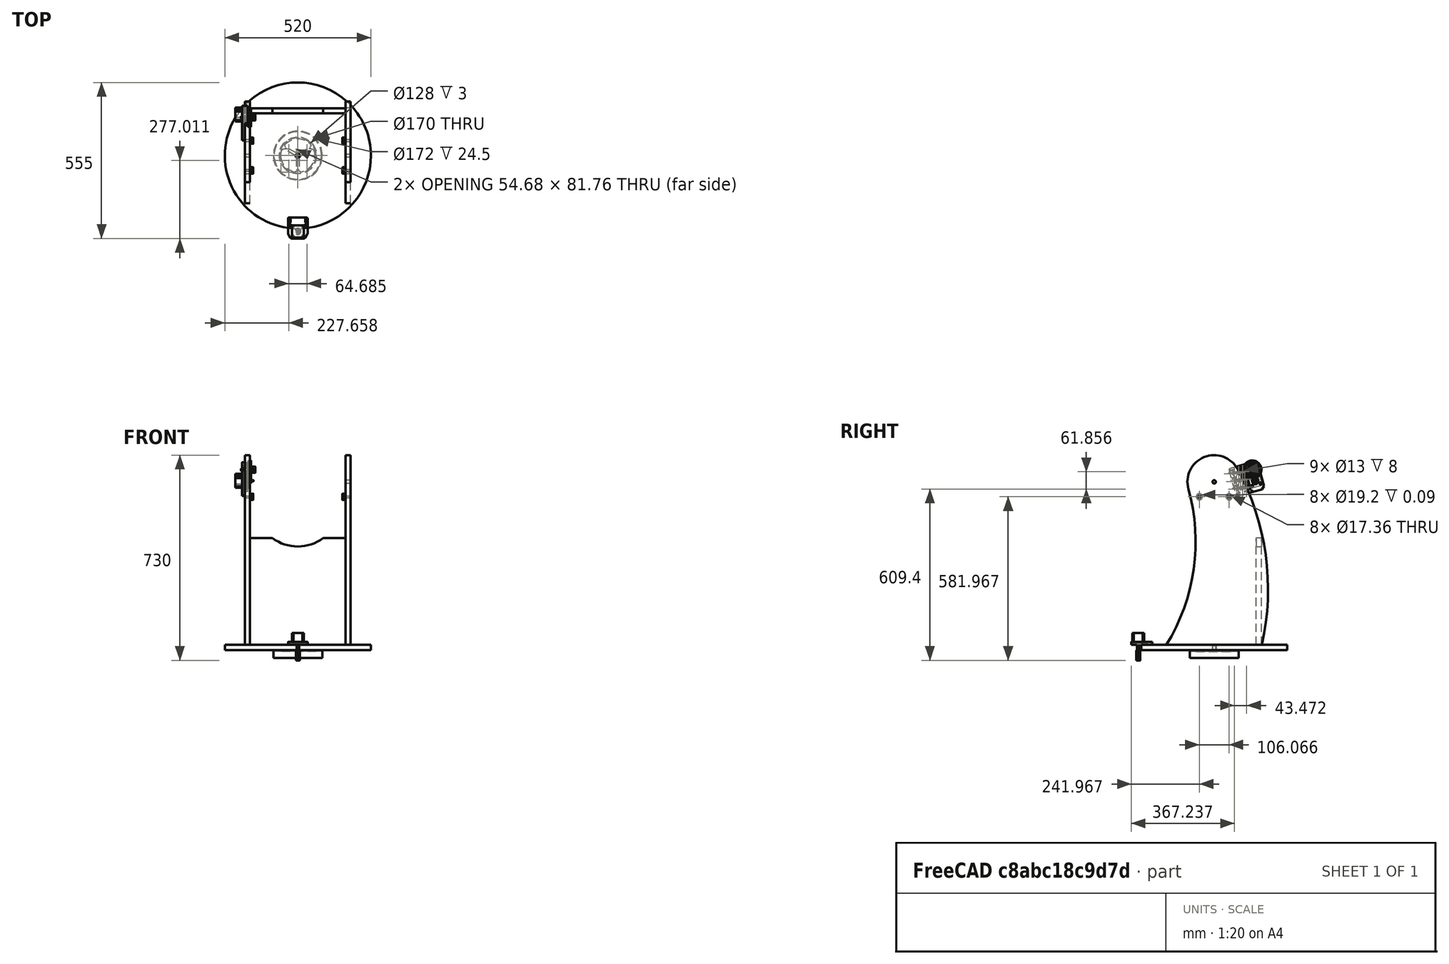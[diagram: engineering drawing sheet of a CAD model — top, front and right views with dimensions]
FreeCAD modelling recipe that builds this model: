
FCSTD DOCUMENT  (FreeCAD 2020.12.13R23076 +3015 (Git))
Label: zawieszenia-gora
License: All rights reserved
LicenseURL: http://en.wikipedia.org/wiki/All_rights_reserved
objects: App::FeaturePython×116, Part::FeaturePython×97, App::Link×24
note: 96 computed .brp shape members not serialized (recipe doc carries the construction recipe); baked Part::Feature solids carry a one-line shape summary decoded from their .brp
EXTERNAL_REF file=plyta-okr-gora.fcstd obj=Body
EXTERNAL_REF file=plyta-tylna.fcstd obj=Body
EXTERNAL_REF file=plyta-boczna.fcstd obj=Body
EXTERNAL_REF file=krokowiec-dol.FCStd obj=Body
EXTERNAL_REF file=krokowiec-nema17.FCStd obj=Body
EXTERNAL_REF file=kolkozebmodul1fi5sc.FCStd obj=Body
EXTERNAL_REF file=przekladnia.FCStd obj=Assembly
EXTERNAL_REF file=tulejka-sruby.FCStd obj=Body
EXTERNAL_REF file=piasta-lozyska2.FCStd obj=Body
EXTERNAL_REF file=oslona-lozyska.FCStd obj=Body
EXTERNAL_REF file=dystans-lozyska.FCStd obj=Body
EXTERNAL_REF file=lozysko 608.FCStd obj=Assembly

FEATURE [App::Link] Link  label="Link_plyta-okr-gora"
  LinkPlacement = pos=(-111,-1.99997,195) rot=(0,0,1;0rad)
  LinkedObject = -> <external plyta-okr-gora.fcstd>#Body
  Placement = pos=(-111,-1.99997,195) rot=(0,0,1;0rad)
  SyncGroupVisibility = false
  _LinkVersion = 1
FEATURE [App::Link] Link001  label="Link001_Assembly"
  LinkedObject = -> Assembly
  SyncGroupVisibility = false
  _LinkVersion = 1
FEATURE [App::Link] Link002  label="Link002_plyta-tylna"
  LinkPlacement = pos=(-111,166,213) rot=(0,0,1;0rad)
  LinkedObject = -> <external plyta-tylna.fcstd>#Body
  Placement = pos=(-111,166,213) rot=(0,0,1;0rad)
  SyncGroupVisibility = false
  _LinkVersion = 1
FEATURE [App::Link] Link003  label="Link003_Assembly"
  LinkedObject = -> Assembly
  SyncGroupVisibility = false
  _LinkVersion = 1
FEATURE [Part::FeaturePython] Element  # link proxy (typed FeaturePython)
  Detach = false
  LinkTransform = true
  LinkedObject = -> Link [Pad.Face2]
  _LinkVersion = 1
FEATURE [Part::FeaturePython] Element001  # link proxy (typed FeaturePython)
  Detach = false
  LinkTransform = true
  LinkedObject = -> Link002 [Pad.Face1]
  _LinkVersion = 1
FEATURE [Part::FeaturePython] Element002  # link proxy (typed FeaturePython)
  Detach = false
  LinkTransform = true
  LinkedObject = -> Link [Pad.Face3]
  _LinkVersion = 1
FEATURE [Part::FeaturePython] Element003  # link proxy (typed FeaturePython)
  Detach = false
  LinkTransform = true
  LinkedObject = -> Link [Origin.YZ_Plane.]
  _LinkVersion = 1
FEATURE [Part::FeaturePython] Element004  # link proxy (typed FeaturePython)
  Detach = false
  LinkTransform = true
  LinkedObject = -> Link002 [Origin.YZ_Plane.]
  _LinkVersion = 1
FEATURE [Part::FeaturePython] Element005  # link proxy (typed FeaturePython)
  Detach = false
  LinkTransform = true
  LinkedObject = -> Link002 [Origin.XY_Plane.]
  _LinkVersion = 1
FEATURE [Part::FeaturePython] Element006  # link proxy (typed FeaturePython)
  Detach = false
  LinkTransform = true
  LinkedObject = -> Link002 [Pad.Face8]
  _LinkVersion = 1
FEATURE [Part::FeaturePython] Element007  # link proxy (typed FeaturePython)
  Detach = false
  LinkTransform = true
  LinkedObject = -> Link [Origin.XZ_Plane.]
  _LinkVersion = 1
FEATURE [App::Link] Link004  label="Link004_Assembly"
  LinkedObject = -> Assembly
  SyncGroupVisibility = false
  _LinkVersion = 1
FEATURE [App::Link] Link005  label="Link005_plyta-boczna"
  LinkPlacement = pos=(68.0001,-1.99997,213) rot=(0,0,1;0rad)
  LinkedObject = -> <external plyta-boczna.fcstd>#Body
  Placement = pos=(68.0001,-1.99997,213) rot=(0,0,1;0rad)
  SyncGroupVisibility = false
  _LinkVersion = 1
FEATURE [Part::FeaturePython] Element008  # link proxy (typed FeaturePython)
  Detach = false
  LinkTransform = true
  LinkedObject = -> Link005 [Pad.Face6]
  _LinkVersion = 1
FEATURE [Part::FeaturePython] Element009  # link proxy (typed FeaturePython)
  Detach = false
  LinkTransform = true
  LinkedObject = -> Link002 [Pad.Face2]
  _LinkVersion = 1
FEATURE [Part::FeaturePython] Element010  # link proxy (typed FeaturePython)
  Detach = false
  LinkTransform = true
  LinkedObject = -> Link005 [Origin.XY_Plane.]
  _LinkVersion = 1
FEATURE [Part::FeaturePython] Element011  # link proxy (typed FeaturePython)
  Detach = false
  LinkTransform = true
  LinkedObject = -> Link005 [Origin.XZ_Plane.]
  _LinkVersion = 1
FEATURE [App::Link] Link006  label="Link006_Assembly"
  LinkedObject = -> Assembly
  SyncGroupVisibility = false
  _LinkVersion = 1
FEATURE [App::Link] Link007  label="Link007_plyta-boczna"
  LinkPlacement = pos=(-290,-1.99997,213) rot=(0,0,1;0rad)
  LinkedObject = -> <external plyta-boczna.fcstd>#Body
  Placement = pos=(-290,-1.99997,213) rot=(0,0,1;0rad)
  SyncGroupVisibility = false
  _LinkVersion = 1
FEATURE [Part::FeaturePython] Element012  # link proxy (typed FeaturePython)
  Detach = false
  LinkTransform = true
  LinkedObject = -> Link007 [Pad.Face7]
  _LinkVersion = 1
FEATURE [Part::FeaturePython] Element013  # link proxy (typed FeaturePython)
  Detach = false
  LinkTransform = true
  LinkedObject = -> Link002 [Pad.Face6]
  _LinkVersion = 1
FEATURE [Part::FeaturePython] Element014  # link proxy (typed FeaturePython)
  Detach = false
  LinkTransform = true
  LinkedObject = -> Link007 [Origin.XY_Plane.]
  _LinkVersion = 1
FEATURE [Part::FeaturePython] Element015  # link proxy (typed FeaturePython)
  Detach = false
  LinkTransform = true
  LinkedObject = -> Link007 [Origin.XZ_Plane.]
  _LinkVersion = 1
FEATURE [App::Link] Link009  label="Link009_zawieszenie-gora"
  LinkedObject = -> Assembly
  SyncGroupVisibility = false
  _LinkVersion = 1
FEATURE [Part::FeaturePython] Element017  # link proxy (typed FeaturePython)
  Detach = false
  LinkTransform = true
  LinkedObject = -> Link005 [Pocket.Face9]
  _LinkVersion = 1
FEATURE [Part::FeaturePython] Element019  # link proxy (typed FeaturePython)
  Detach = false
  LinkTransform = true
  LinkedObject = -> Link005 [Pocket.Face4]
  _LinkVersion = 1
FEATURE [Part::FeaturePython] Element020  # link proxy (typed FeaturePython)
  Detach = false
  LinkTransform = true
  LinkedObject = -> Link005 [Pocket.Face8]
  _LinkVersion = 1
FEATURE [Part::FeaturePython] Element024  # link proxy (typed FeaturePython)
  Detach = false
  LinkTransform = true
  LinkedObject = -> Link005 [Pocket.Face1]
  _LinkVersion = 1
FEATURE [App::Link] Link010  label="krokowiec-dol"
  LinkPlacement = pos=(-111,-272,213) rot=(0,0,1;0rad)
  LinkedObject = -> <external krokowiec-dol.FCStd>#Body
  Placement = pos=(-111,-272,213) rot=(0,0,1;0rad)
  SyncGroupVisibility = false
  _LinkVersion = 1
FEATURE [App::Link] Link011  label="nema17"
  LinkPlacement = pos=(-111,-272,256) rot=(1,0,0;3.14159rad)
  LinkedObject = -> <external krokowiec-nema17.FCStd>#Body
  Placement = pos=(-111,-272,256) rot=(1,0,0;3.14159rad)
  SyncGroupVisibility = false
  _LinkVersion = 1
FEATURE [App::Link] Link012  label="kolkozebstoz"
  LinkPlacement = pos=(-111,-272,158) rot=(0,0,1;0rad)
  LinkedObject = -> <external kolkozebmodul1fi5sc.FCStd>#Body
  Placement = pos=(-111,-272,158) rot=(0,0,1;0rad)
  SyncGroupVisibility = false
  _LinkVersion = 1
FEATURE [App::Link] Link016  label="przekladnia"
  LinkPlacement = pos=(-309,143.893,797.746) rot=(-0.704063,-0.092692,0.704063;2.95674rad)
  LinkedObject = -> <external przekladnia.FCStd>#Assembly
  Placement = pos=(-309,143.893,797.746) rot=(-0.704063,-0.092692,0.704063;2.95674rad)
  SyncGroupVisibility = false
  _LinkVersion = 1
FEATURE [App::Link] Link017  label="tulejka-sruby"
  LinkPlacement = pos=(-111,-1.99997,195) rot=(0,0,1;0rad)
  LinkedObject = -> <external tulejka-sruby.FCStd>#Body
  Placement = pos=(-111,-1.99997,195) rot=(0,0,1;0rad)
  SyncGroupVisibility = false
  _LinkVersion = 1
FEATURE [App::Link] Link018  label="piasta-lozyska2"
  LinkPlacement = pos=(-111,-1.99997,195) rot=(1,0,0;3.14159rad)
  LinkedObject = -> <external piasta-lozyska2.FCStd>#Body
  Placement = pos=(-111,-1.99997,195) rot=(1,0,0;3.14159rad)
  SyncGroupVisibility = false
  _LinkVersion = 1
FEATURE [App::Link] Link019  label="oslona-lozyska"
  LinkPlacement = pos=(-111,-1.99997,166) rot=(0,0,1;0rad)
  LinkedObject = -> <external oslona-lozyska.FCStd>#Body
  Placement = pos=(-111,-1.99997,166) rot=(0,0,1;0rad)
  SyncGroupVisibility = false
  _LinkVersion = 1
FEATURE [App::Link] Link020  label="dystans-lozyska"
  LinkPlacement = pos=(-281,-55.033,739.967) rot=(0.678598,0.281085,0.678598;2.59356rad)
  LinkedObject = -> <external dystans-lozyska.FCStd>#Body
  Placement = pos=(-281,-55.033,739.967) rot=(0.678598,0.281085,0.678598;2.59356rad)
  SyncGroupVisibility = false
  _LinkVersion = 1
FEATURE [App::Link] Link021  label="dystans-lozyska001"
  LinkPlacement = pos=(-281,51.033,739.967) rot=(0.678598,-0.281085,0.678598;3.68962rad)
  LinkedObject = -> Link020
  Placement = pos=(-281,51.033,739.967) rot=(0.678598,-0.281085,0.678598;3.68962rad)
  SyncGroupVisibility = false
  _LinkVersion = 1
FEATURE [App::Link] Link022  label="dystans-lozyska002"
  LinkPlacement = pos=(59.0001,-55.033,739.967) rot=(-0.357407,-0.862856,0.357407;1.71777rad)
  LinkedObject = -> Link020
  Placement = pos=(59.0001,-55.033,739.967) rot=(-0.357407,-0.862856,0.357407;1.71777rad)
  SyncGroupVisibility = false
  _LinkVersion = 1
FEATURE [App::Link] Link023  label="dystans-lozyska003"
  LinkPlacement = pos=(59.0001,51.033,739.967) rot=(-0.357407,0.862856,0.357407;4.56541rad)
  LinkedObject = -> Link020
  Placement = pos=(59.0001,51.033,739.967) rot=(-0.357407,0.862856,0.357407;4.56541rad)
  SyncGroupVisibility = false
  _LinkVersion = 1
FEATURE [App::Link] Link024  label="608-2RS"
  LinkPlacement = pos=(-277,-55.033,739.967) rot=(0,0,1;0rad)
  LinkedObject = -> <external lozysko 608.FCStd>#Assembly
  Placement = pos=(-277,-55.033,739.967) rot=(0,0,1;0rad)
  SyncGroupVisibility = false
  _LinkVersion = 1
FEATURE [App::Link] Link026  label="608-2RS002"
  LinkPlacement = pos=(-277,51.033,739.967) rot=(0,0,1;0rad)
  LinkedObject = -> Link024
  Placement = pos=(-277,51.033,739.967) rot=(0,0,1;0rad)
  SyncGroupVisibility = false
  _LinkVersion = 1
FEATURE [App::Link] Link027  label="608-2RS003"
  LinkPlacement = pos=(55.0001,-55.033,739.967) rot=(0,1,0;3.14159rad)
  LinkedObject = -> Link024
  Placement = pos=(55.0001,-55.033,739.967) rot=(0,1,0;3.14159rad)
  SyncGroupVisibility = false
  _LinkVersion = 1
FEATURE [App::Link] Link028  label="608-2RS004"
  LinkPlacement = pos=(55.0001,51.033,739.967) rot=(0,1,0;3.14159rad)
  LinkedObject = -> Link024
  Placement = pos=(55.0001,51.033,739.967) rot=(0,1,0;3.14159rad)
  SyncGroupVisibility = false
  _LinkVersion = 1
FEATURE [Part::FeaturePython] Parts  # WARN: FeaturePython — macro-defined, semantics opaque (R4)
  Group = -> [Link,Link002,Link005,Link007,Link010,Link011,Link012,Link016,Link017,Link018,Link019,Link020,Link021,Link022,Link023,Link024,Link026,Link027,Link028]
  GroupMode = 0
  _LinkVersion = 1
FEATURE [Part::FeaturePython] Assembly  label="zawieszenie-gora"  # WARN: FeaturePython — macro-defined, semantics opaque (R4)
  AutoRelax = true
  BuildShape = 0
  Freeze = true
  Group = -> [Constraints,Elements,Parts]
  Verbose = false
  _LinkVersion = 1
  _SolverType = 1
FEATURE [App::FeaturePython] Constraints  # WARN: FeaturePython — macro-defined, semantics opaque (R4)
  Group = -> [Constraint,Constraint001,Constraint002,Constraint003,Constraint004,Constraint005,Constraint006,Constraint007,Constraint008,Constraint013,Constraint014,Constraint015,Constraint022,Constraint023,Constraint024,Constraint025,Constraint026,Constraint027,Constraint028,Constraint029,Constraint030,Constraint031,Constraint032,Constraint033,Constraint034,Constraint035,Constraint036,Constraint037,+10 more]
  _LinkVersion = 1
  _Version = 1
FEATURE [App::FeaturePython] Elements  # WARN: FeaturePython — macro-defined, semantics opaque (R4)
  Group = -> [Element,Element001,Element002,Element003,Element004,Element005,Element006,Element007,Element008,Element009,Element010,Element011,Element012,Element013,Element014,Element015,Element017,Element019,Element020,Element024,Element025,Element026,Element027,Element028,_Element,_Element001,_Element002,_Element003,_Element004,_Element005,_Element006,_Element007,_Element008,Element029,Element030,Element031,+59 more]
  _LinkVersion = 1
FEATURE [Part::FeaturePython] Element025  # link proxy (typed FeaturePython)
  Detach = false
  LinkTransform = true
  LinkedObject = -> Link [Pocket.Face4]
  _LinkVersion = 1
  _Parent = -> Elements
FEATURE [Part::FeaturePython] Element026  # link proxy (typed FeaturePython)
  Detach = false
  LinkTransform = true
  LinkedObject = -> Link [Pocket.Edge4]
  _LinkVersion = 1
  _Parent = -> Elements
FEATURE [Part::FeaturePython] Element027  # link proxy (typed FeaturePython)
  Detach = false
  LinkTransform = true
  LinkedObject = -> Link [Pocket.Face2]
  _LinkVersion = 1
  _Parent = -> Elements
FEATURE [Part::FeaturePython] Element028  # link proxy (typed FeaturePython)
  Detach = false
  LinkTransform = true
  LinkedObject = -> Link007 [Pocket.Edge17]
  _LinkVersion = 1
  _Parent = -> Elements
FEATURE [App::FeaturePython] Constraint  label="PlaneAlignment"  # WARN: FeaturePython — macro-defined, semantics opaque (R4)
  Angle = 0
  AnglePitch = 0
  AngleRoll = 0
  Cascade = false
  Disabled = false
  Group = -> [ElementLink,ElementLink001]
  LockAngle = false
  _ConstraintType = 37
  _LinkVersion = 1
  _Parent = -> Constraints
FEATURE [App::FeaturePython] ElementLink  label="Element001"  # link proxy (typed FeaturePython)
  LinkTransform = true
  LinkedObject = -> Element001
  _LinkVersion = 1
  _Parent = -> Constraint
FEATURE [App::FeaturePython] ElementLink001  label="_Element"  # link proxy (typed FeaturePython)
  LinkTransform = true
  LinkedObject = -> _Element
  _LinkVersion = 1
  _Parent = -> Constraint
FEATURE [Part::FeaturePython] _Element  # link proxy (typed FeaturePython)
  Detach = false
  LinkTransform = true
  LinkedObject = -> Link [Pocket.Face3]
  _LinkVersion = 1
  _Parent = -> Elements
FEATURE [Part::FeaturePython] _Element001  # link proxy (typed FeaturePython)
  Detach = false
  LinkTransform = true
  LinkedObject = -> Link [Sketch002.Edge2]
  _LinkVersion = 1
  _Parent = -> Elements
FEATURE [Part::FeaturePython] _Element002  # link proxy (typed FeaturePython)
  Detach = false
  LinkTransform = true
  LinkedObject = -> Link [Sketch002.Vertex1]
  _LinkVersion = 1
  _Parent = -> Elements
FEATURE [App::FeaturePython] Constraint001  label="PointInPlane"  # WARN: FeaturePython — macro-defined, semantics opaque (R4)
  Disabled = false
  Group = -> [ElementLink002,ElementLink003]
  _ConstraintType = 3
  _LinkVersion = 1
  _Parent = -> Constraints
FEATURE [App::FeaturePython] ElementLink002  label="_Element002"  # link proxy (typed FeaturePython)
  LinkTransform = true
  LinkedObject = -> _Element002
  _LinkVersion = 1
  _Parent = -> Constraint001
FEATURE [App::FeaturePython] ElementLink003  label="Element006"  # link proxy (typed FeaturePython)
  LinkTransform = true
  LinkedObject = -> Element006
  _LinkVersion = 1
  _Parent = -> Constraint001
FEATURE [App::FeaturePython] Constraint002  label="PointInPlane001"  # WARN: FeaturePython — macro-defined, semantics opaque (R4)
  Disabled = false
  Group = -> [ElementLink004,ElementLink005]
  _ConstraintType = 3
  _LinkVersion = 1
  _Parent = -> Constraints
FEATURE [App::FeaturePython] ElementLink004  label="_Element003"  # link proxy (typed FeaturePython)
  LinkTransform = true
  LinkedObject = -> _Element003
  _LinkVersion = 1
  _Parent = -> Constraint002
FEATURE [Part::FeaturePython] _Element003  # link proxy (typed FeaturePython)
  Detach = false
  LinkTransform = true
  LinkedObject = -> Link [Sketch002.Vertex3]
  _LinkVersion = 1
  _Parent = -> Elements
FEATURE [App::FeaturePython] ElementLink005  label="Element006"  # link proxy (typed FeaturePython)
  LinkTransform = true
  LinkedObject = -> Element006
  _LinkVersion = 1
  _Parent = -> Constraint002
FEATURE [App::FeaturePython] Constraint003  label="PlaneAlignment001"  # WARN: FeaturePython — macro-defined, semantics opaque (R4)
  Angle = 0
  AnglePitch = 0
  AngleRoll = 0
  Cascade = false
  Disabled = false
  Group = -> [ElementLink006,ElementLink007]
  LockAngle = false
  _ConstraintType = 37
  _LinkVersion = 1
  _Parent = -> Constraints
FEATURE [App::FeaturePython] ElementLink006  label="_Element004"  # link proxy (typed FeaturePython)
  LinkTransform = true
  LinkedObject = -> _Element004
  _LinkVersion = 1
  _Parent = -> Constraint003
FEATURE [Part::FeaturePython] _Element004  # link proxy (typed FeaturePython)
  Detach = false
  LinkTransform = true
  LinkedObject = -> Link005 [Pocket.Face6]
  _LinkVersion = 1
  _Parent = -> Elements
FEATURE [App::FeaturePython] ElementLink007  label="_Element"  # link proxy (typed FeaturePython)
  LinkTransform = true
  LinkedObject = -> _Element
  _LinkVersion = 1
  _Parent = -> Constraint003
FEATURE [App::FeaturePython] Constraint004  label="PointOnLine"  # WARN: FeaturePython — macro-defined, semantics opaque (R4)
  Disabled = false
  Group = -> [ElementLink008,ElementLink009]
  _ConstraintType = 4
  _LinkVersion = 1
  _Parent = -> Constraints
FEATURE [App::FeaturePython] ElementLink008  label="_Element005"  # link proxy (typed FeaturePython)
  LinkTransform = true
  LinkedObject = -> _Element005
  _LinkVersion = 1
  _Parent = -> Constraint004
FEATURE [Part::FeaturePython] _Element005  # link proxy (typed FeaturePython)
  Detach = false
  LinkTransform = true
  LinkedObject = -> Link [Sketch002.Vertex2]
  _LinkVersion = 1
  _Parent = -> Elements
FEATURE [App::FeaturePython] ElementLink009  label="_Element006"  # link proxy (typed FeaturePython)
  LinkTransform = true
  LinkedObject = -> _Element006
  _LinkVersion = 1
  _Parent = -> Constraint004
FEATURE [Part::FeaturePython] _Element006  # link proxy (typed FeaturePython)
  Detach = false
  LinkTransform = true
  LinkedObject = -> Link007 [Sketch002.Edge1]
  _LinkVersion = 1
  _Parent = -> Elements
FEATURE [App::FeaturePython] Constraint005  label="PlaneAlignment002"  # WARN: FeaturePython — macro-defined, semantics opaque (R4)
  Angle = 0
  AnglePitch = 0
  AngleRoll = 0
  Cascade = false
  Disabled = false
  Group = -> [ElementLink010,ElementLink011]
  LockAngle = false
  _ConstraintType = 37
  _LinkVersion = 1
  _Parent = -> Constraints
FEATURE [App::FeaturePython] ElementLink010  label="_Element007"  # link proxy (typed FeaturePython)
  LinkTransform = true
  LinkedObject = -> _Element007
  _LinkVersion = 1
  _Parent = -> Constraint005
FEATURE [Part::FeaturePython] _Element007  # link proxy (typed FeaturePython)
  Detach = false
  LinkTransform = true
  LinkedObject = -> Link007 [Pocket.Face6]
  _LinkVersion = 1
  _Parent = -> Elements
FEATURE [App::FeaturePython] ElementLink011  label="_Element"  # link proxy (typed FeaturePython)
  LinkTransform = true
  LinkedObject = -> _Element
  _LinkVersion = 1
  _Parent = -> Constraint005
FEATURE [App::FeaturePython] Constraint006  label="AxialAlignment"  # WARN: FeaturePython — macro-defined, semantics opaque (R4)
  Angle = 0
  AnglePitch = 0
  AngleRoll = 0
  Disabled = false
  Group = -> [ElementLink012,ElementLink013]
  LockAngle = false
  Multiply = false
  _ConstraintType = 36
  _LinkVersion = 1
  _Parent = -> Constraints
FEATURE [App::FeaturePython] ElementLink012  label="_Element008"  # link proxy (typed FeaturePython)
  LinkTransform = true
  LinkedObject = -> _Element008
  _LinkVersion = 1
  _Parent = -> Constraint006
FEATURE [Part::FeaturePython] _Element008  # link proxy (typed FeaturePython)
  Detach = false
  LinkTransform = true
  LinkedObject = -> Link007 [Pocket.Face1]
  _LinkVersion = 1
  _Parent = -> Elements
FEATURE [App::FeaturePython] ElementLink013  label="Element024"  # link proxy (typed FeaturePython)
  LinkTransform = true
  LinkedObject = -> Element024
  _LinkVersion = 1
  _Parent = -> Constraint006
FEATURE [Part::FeaturePython] Element029  # link proxy (typed FeaturePython)
  Detach = false
  LinkTransform = true
  LinkedObject = -> Link007 [Pocket.Face8]
  _LinkVersion = 1
  _Parent = -> Elements
FEATURE [Part::FeaturePython] Element030  # link proxy (typed FeaturePython)
  Detach = false
  LinkTransform = true
  LinkedObject = -> Link007 [Pocket.Face5]
  _LinkVersion = 1
  _Parent = -> Elements
FEATURE [Part::FeaturePython] Element031  # link proxy (typed FeaturePython)
  Detach = false
  LinkTransform = true
  LinkedObject = -> Link007 [Sketch002.Vertex1]
  _LinkVersion = 1
  _Parent = -> Elements
FEATURE [App::FeaturePython] Constraint007  label="PointsCoincident"  # WARN: FeaturePython — macro-defined, semantics opaque (R4)
  Disabled = false
  Group = -> [ElementLink014,ElementLink015]
  _ConstraintType = 1
  _LinkVersion = 1
  _Parent = -> Constraints
FEATURE [App::FeaturePython] ElementLink014  label="_Element009"  # link proxy (typed FeaturePython)
  LinkTransform = true
  LinkedObject = -> _Element009
  _LinkVersion = 1
  _Parent = -> Constraint007
FEATURE [Part::FeaturePython] _Element009  # link proxy (typed FeaturePython)
  Detach = false
  LinkTransform = true
  LinkedObject = -> Link [Sketch002.Vertex6]
  _LinkVersion = 1
  _Parent = -> Elements
FEATURE [App::FeaturePython] ElementLink015  label="_Element010"  # link proxy (typed FeaturePython)
  LinkTransform = true
  LinkedObject = -> _Element010
  _LinkVersion = 1
  _Parent = -> Constraint007
FEATURE [Part::FeaturePython] _Element010  # link proxy (typed FeaturePython)
  Detach = false
  LinkTransform = true
  LinkedObject = -> Link010 [Sketch008.Vertex2]
  _LinkVersion = 1
  _Parent = -> Elements
FEATURE [App::FeaturePython] Constraint008  label="PointOnLine001"  # WARN: FeaturePython — macro-defined, semantics opaque (R4)
  Disabled = false
  Group = -> [ElementLink016,ElementLink017]
  _ConstraintType = 4
  _LinkVersion = 1
  _Parent = -> Constraints
FEATURE [App::FeaturePython] ElementLink016  label="_Element011"  # link proxy (typed FeaturePython)
  LinkTransform = true
  LinkedObject = -> _Element011
  _LinkVersion = 1
  _Parent = -> Constraint008
FEATURE [Part::FeaturePython] _Element011  # link proxy (typed FeaturePython)
  Detach = false
  LinkTransform = true
  LinkedObject = -> Link010 [Sketch008.Vertex1]
  _LinkVersion = 1
  _Parent = -> Elements
FEATURE [App::FeaturePython] ElementLink017  label="_Element012"  # link proxy (typed FeaturePython)
  LinkTransform = true
  LinkedObject = -> _Element012
  _LinkVersion = 1
  _Parent = -> Constraint008
FEATURE [Part::FeaturePython] _Element012  # link proxy (typed FeaturePython)
  Detach = false
  LinkTransform = true
  LinkedObject = -> Link [Sketch002.Edge4]
  _LinkVersion = 1
  _Parent = -> Elements
FEATURE [Part::FeaturePython] _Element013  # link proxy (typed FeaturePython)
  Detach = false
  LinkTransform = true
  LinkedObject = -> Link011 [Chamfer001.Face9]
  _LinkVersion = 1
  _Parent = -> Elements
FEATURE [Part::FeaturePython] _Element015  # link proxy (typed FeaturePython)
  Detach = false
  LinkTransform = true
  LinkedObject = -> Link011 [Chamfer001.Face13]
  _LinkVersion = 1
  _Parent = -> Elements
FEATURE [Part::FeaturePython] _Element018  # link proxy (typed FeaturePython)
  Detach = false
  LinkTransform = true
  LinkedObject = -> Link011 [Chamfer001.Face1]
  _LinkVersion = 1
  _Parent = -> Elements
FEATURE [Part::FeaturePython] _Element020  # link proxy (typed FeaturePython)
  Detach = false
  LinkTransform = true
  LinkedObject = -> Link012 [Groove.Face75]
  _LinkVersion = 1
  _Parent = -> Elements
FEATURE [Part::FeaturePython] _Element021  # link proxy (typed FeaturePython)
  Detach = false
  LinkTransform = true
  LinkedObject = -> Link011 [Chamfer001.Face21]
  _LinkVersion = 1
  _Parent = -> Elements
FEATURE [Part::FeaturePython] _Element022  # link proxy (typed FeaturePython)
  Detach = false
  LinkTransform = true
  LinkedObject = -> Link012 [Groove.Face78]
  _LinkVersion = 1
  _Parent = -> Elements
FEATURE [Part::FeaturePython] _Element023  # link proxy (typed FeaturePython)
  Detach = false
  LinkTransform = true
  LinkedObject = -> Link011 [Chamfer001.Face23]
  _LinkVersion = 1
  _Parent = -> Elements
FEATURE [Part::FeaturePython] _Element024  # link proxy (typed FeaturePython)
  Detach = false
  LinkTransform = true
  LinkedObject = -> Link012 [Groove.Face76]
  _LinkVersion = 1
  _Parent = -> Elements
FEATURE [Part::FeaturePython] _Element025  # link proxy (typed FeaturePython)
  Detach = false
  LinkTransform = true
  LinkedObject = -> Link011 [Chamfer001.Face22]
  _LinkVersion = 1
  _Parent = -> Elements
FEATURE [Part::FeaturePython] _Element026  # link proxy (typed FeaturePython)
  Detach = false
  LinkTransform = true
  LinkedObject = -> Link011 [Chamfer001.Vertex1]
  _LinkVersion = 1
  _Parent = -> Elements
FEATURE [App::FeaturePython] Constraint013  label="AxialAlignment002"  # WARN: FeaturePython — macro-defined, semantics opaque (R4)
  Angle = 0
  AnglePitch = 0
  AngleRoll = 0
  Disabled = false
  Group = -> [ElementLink026,ElementLink027]
  LockAngle = false
  Multiply = false
  _ConstraintType = 36
  _LinkVersion = 1
  _Parent = -> Constraints
FEATURE [App::FeaturePython] ElementLink026  label="_Element020"  # link proxy (typed FeaturePython)
  LinkTransform = true
  LinkedObject = -> _Element020
  _LinkVersion = 1
  _Parent = -> Constraint013
FEATURE [App::FeaturePython] ElementLink027  label="_Element021"  # link proxy (typed FeaturePython)
  LinkTransform = true
  LinkedObject = -> _Element021
  _LinkVersion = 1
  _Parent = -> Constraint013
FEATURE [App::FeaturePython] Constraint014  label="SameOrientation002"  # WARN: FeaturePython — macro-defined, semantics opaque (R4)
  Disabled = false
  Group = -> [ElementLink028,ElementLink029]
  _ConstraintType = 2
  _LinkVersion = 1
  _Parent = -> Constraints
FEATURE [App::FeaturePython] ElementLink028  label="_Element022"  # link proxy (typed FeaturePython)
  LinkTransform = true
  LinkedObject = -> _Element022
  _LinkVersion = 1
  _Parent = -> Constraint014
FEATURE [App::FeaturePython] ElementLink029  label="_Element023"  # link proxy (typed FeaturePython)
  LinkTransform = true
  LinkedObject = -> _Element023
  _LinkVersion = 1
  _Parent = -> Constraint014
FEATURE [App::FeaturePython] Constraint015  label="PointInPlane003"  # WARN: FeaturePython — macro-defined, semantics opaque (R4)
  Disabled = false
  Group = -> [ElementLink030,ElementLink031]
  _ConstraintType = 3
  _LinkVersion = 1
  _Parent = -> Constraints
FEATURE [App::FeaturePython] ElementLink030  label="_Element027"  # link proxy (typed FeaturePython)
  LinkTransform = true
  LinkedObject = -> _Element027
  _LinkVersion = 1
  _Parent = -> Constraint015
FEATURE [Part::FeaturePython] _Element027  # link proxy (typed FeaturePython)
  Detach = false
  LinkTransform = true
  LinkedObject = -> Link011 [Chamfer001.Vertex33]
  _LinkVersion = 1
  _Parent = -> Elements
FEATURE [App::FeaturePython] ElementLink031  label="_Element024"  # link proxy (typed FeaturePython)
  LinkTransform = true
  LinkedObject = -> _Element024
  _LinkVersion = 1
  _Parent = -> Constraint015
FEATURE [Part::FeaturePython] _Element033  # link proxy (typed FeaturePython)
  Detach = false
  LinkTransform = true
  LinkedObject = -> Link007 [Pocket.Face4]
  _LinkVersion = 1
  _Parent = -> Elements
FEATURE [App::FeaturePython] Constraint022  label="PointInPlane006"  # WARN: FeaturePython — macro-defined, semantics opaque (R4)
  Disabled = false
  Group = -> [ElementLink044,ElementLink045]
  _ConstraintType = 3
  _LinkVersion = 1
  _Parent = -> Constraints
FEATURE [App::FeaturePython] ElementLink044  label="_Element002"  # link proxy (typed FeaturePython)
  LinkTransform = true
  LinkedObject = -> _Element002
  _LinkVersion = 1
  _Parent = -> Constraint022
FEATURE [App::FeaturePython] ElementLink045  label="Element030"  # link proxy (typed FeaturePython)
  LinkTransform = true
  LinkedObject = -> Element030
  _LinkVersion = 1
  _Parent = -> Constraint022
FEATURE [App::FeaturePython] Constraint023  label="PlaneAlignment003"  # WARN: FeaturePython — macro-defined, semantics opaque (R4)
  Angle = 0
  AnglePitch = 0
  AngleRoll = 0
  Cascade = false
  Disabled = false
  Group = -> [ElementLink046,ElementLink047]
  LockAngle = false
  _ConstraintType = 37
  _LinkVersion = 1
  _Parent = -> Constraints
FEATURE [App::FeaturePython] ElementLink046  label="Element013"  # link proxy (typed FeaturePython)
  LinkTransform = true
  LinkedObject = -> Element013
  _LinkVersion = 1
  _Parent = -> Constraint023
FEATURE [App::FeaturePython] ElementLink047  label="Element030"  # link proxy (typed FeaturePython)
  LinkTransform = true
  LinkedObject = -> Element030
  _LinkVersion = 1
  _Parent = -> Constraint023
FEATURE [App::FeaturePython] Constraint024  label="PlaneAlignment004"  # WARN: FeaturePython — macro-defined, semantics opaque (R4)
  Angle = 0
  AnglePitch = 0
  AngleRoll = 0
  Cascade = false
  Disabled = false
  Group = -> [ElementLink048,ElementLink049]
  LockAngle = false
  _ConstraintType = 37
  _LinkVersion = 1
  _Parent = -> Constraints
FEATURE [App::FeaturePython] ElementLink048  label="Element019"  # link proxy (typed FeaturePython)
  LinkTransform = true
  LinkedObject = -> Element019
  _LinkVersion = 1
  _Parent = -> Constraint024
FEATURE [App::FeaturePython] ElementLink049  label="Element009"  # link proxy (typed FeaturePython)
  LinkTransform = true
  LinkedObject = -> Element009
  _LinkVersion = 1
  _Parent = -> Constraint024
FEATURE [Part::FeaturePython] _Element053  # link proxy (typed FeaturePython)
  Detach = false
  LinkTransform = true
  LinkedObject = -> Link016 [1.$_Element003.]
  _LinkVersion = 1
  _Parent = -> Elements
FEATURE [Part::FeaturePython] _Element055  # link proxy (typed FeaturePython)
  Detach = false
  LinkTransform = true
  LinkedObject = -> Link016 [1.$_Element.]
  _LinkVersion = 1
  _Parent = -> Elements
FEATURE [App::FeaturePython] Constraint025  label="PlaneCoincident"  # WARN: FeaturePython — macro-defined, semantics opaque (R4)
  Angle = 0
  AnglePitch = 0
  AngleRoll = 0
  Cascade = false
  Disabled = false
  Group = -> [ElementLink050,ElementLink051]
  LockAngle = false
  Multiply = false
  OffsetX = 0
  OffsetY = 0
  _ConstraintType = 35
  _LinkVersion = 1
  _Parent = -> Constraints
FEATURE [App::FeaturePython] ElementLink050  label="_Element056"  # link proxy (typed FeaturePython)
  LinkTransform = true
  LinkedObject = -> _Element056
  _LinkVersion = 1
  _Parent = -> Constraint025
FEATURE [Part::FeaturePython] _Element056  # link proxy (typed FeaturePython)
  Detach = false
  LinkTransform = true
  LinkedObject = -> Link017 [Chamfer.Face3]
  _LinkVersion = 1
  _Parent = -> Elements
FEATURE [App::FeaturePython] ElementLink051  label="Element027"  # link proxy (typed FeaturePython)
  LinkTransform = true
  LinkedObject = -> Element027
  _LinkVersion = 1
  _Parent = -> Constraint025
FEATURE [App::FeaturePython] Constraint026  label="PlaneCoincident001"  # WARN: FeaturePython — macro-defined, semantics opaque (R4)
  Angle = 0
  AnglePitch = 0
  AngleRoll = 0
  Cascade = false
  Disabled = false
  Group = -> [ElementLink052,ElementLink053]
  LockAngle = false
  Multiply = false
  OffsetX = 0
  OffsetY = 0
  _ConstraintType = 35
  _LinkVersion = 1
  _Parent = -> Constraints
FEATURE [App::FeaturePython] ElementLink052  label="_Element057"  # link proxy (typed FeaturePython)
  LinkTransform = true
  LinkedObject = -> _Element057
  _LinkVersion = 1
  _Parent = -> Constraint026
FEATURE [Part::FeaturePython] _Element057  # link proxy (typed FeaturePython)
  Detach = false
  LinkTransform = true
  LinkedObject = -> Link018 [Pocket002.Face1]
  _LinkVersion = 1
  _Parent = -> Elements
FEATURE [App::FeaturePython] ElementLink053  label="Element027"  # link proxy (typed FeaturePython)
  LinkTransform = true
  LinkedObject = -> Element027
  _LinkVersion = 1
  _Parent = -> Constraint026
FEATURE [App::FeaturePython] Constraint027  label="PlaneCoincident002"  # WARN: FeaturePython — macro-defined, semantics opaque (R4)
  Angle = 0
  AnglePitch = 0
  AngleRoll = 0
  Cascade = false
  Disabled = false
  Group = -> [ElementLink054,ElementLink055]
  LockAngle = false
  Multiply = false
  OffsetX = 0
  OffsetY = 0
  _ConstraintType = 35
  _LinkVersion = 1
  _Parent = -> Constraints
FEATURE [App::FeaturePython] ElementLink054  label="Element027"  # link proxy (typed FeaturePython)
  LinkTransform = true
  LinkedObject = -> Element027
  _LinkVersion = 1
  _Parent = -> Constraint027
FEATURE [App::FeaturePython] ElementLink055  label="_Element058"  # link proxy (typed FeaturePython)
  LinkTransform = true
  LinkedObject = -> _Element058
  _LinkVersion = 1
  _Parent = -> Constraint027
FEATURE [Part::FeaturePython] _Element058  # link proxy (typed FeaturePython)
  Detach = false
  LinkTransform = true
  LinkedObject = -> Link019 [Chamfer.Face5]
  _LinkVersion = 1
  _Parent = -> Elements
FEATURE [Part::FeaturePython] _Element059  # link proxy (typed FeaturePython)
  Detach = false
  LinkTransform = true
  LinkedObject = -> Link020 [Chamfer001.Edge21]
  _LinkVersion = 1
  _Parent = -> Elements
FEATURE [Part::FeaturePython] _Element060  # link proxy (typed FeaturePython)
  Detach = false
  LinkTransform = true
  LinkedObject = -> Link007 [Pocket.Edge18]
  _LinkVersion = 1
  _Parent = -> Elements
FEATURE [Part::FeaturePython] _Element061  # link proxy (typed FeaturePython)
  Detach = false
  LinkTransform = true
  LinkedObject = -> Link020 [Chamfer001.Face5]
  _LinkVersion = 1
  _Parent = -> Elements
FEATURE [Part::FeaturePython] _Element062  # link proxy (typed FeaturePython)
  Detach = false
  LinkTransform = true
  LinkedObject = -> Link007 [Pocket.Face9]
  _LinkVersion = 1
  _Parent = -> Elements
FEATURE [App::FeaturePython] Constraint028  label="AxialAlignment003"  # WARN: FeaturePython — macro-defined, semantics opaque (R4)
  Angle = -45
  AnglePitch = 0
  AngleRoll = 0
  Disabled = false
  Group = -> [ElementLink056,ElementLink057]
  LockAngle = true
  Multiply = false
  _ConstraintType = 36
  _LinkVersion = 1
  _Parent = -> Constraints
FEATURE [App::FeaturePython] ElementLink056  label="_Element063"  # link proxy (typed FeaturePython)
  LinkTransform = true
  LinkedObject = -> _Element063
  _LinkVersion = 1
  _Parent = -> Constraint028
FEATURE [Part::FeaturePython] _Element063  # link proxy (typed FeaturePython)
  Detach = false
  LinkTransform = true
  LinkedObject = -> Link020 [Chamfer001.Face20]
  _LinkVersion = 1
  _Parent = -> Elements
FEATURE [App::FeaturePython] ElementLink057  label="_Element062"  # link proxy (typed FeaturePython)
  LinkTransform = true
  LinkedObject = -> _Element062
  _LinkVersion = 1
  _Parent = -> Constraint028
FEATURE [App::FeaturePython] Constraint029  label="PointInPlane007"  # WARN: FeaturePython — macro-defined, semantics opaque (R4)
  Disabled = false
  Group = -> [ElementLink058,ElementLink059]
  _ConstraintType = 3
  _LinkVersion = 1
  _Parent = -> Constraints
FEATURE [App::FeaturePython] ElementLink058  label="_Element064"  # link proxy (typed FeaturePython)
  LinkTransform = true
  LinkedObject = -> _Element064
  _LinkVersion = 1
  _Parent = -> Constraint029
FEATURE [Part::FeaturePython] _Element064  # link proxy (typed FeaturePython)
  Detach = false
  LinkTransform = true
  LinkedObject = -> Link020 [Chamfer001.Vertex27]
  _LinkVersion = 1
  _Parent = -> Elements
FEATURE [App::FeaturePython] ElementLink059  label="Element030"  # link proxy (typed FeaturePython)
  LinkTransform = true
  LinkedObject = -> Element030
  _LinkVersion = 1
  _Parent = -> Constraint029
FEATURE [App::FeaturePython] Constraint030  label="AxialAlignment004"  # WARN: FeaturePython — macro-defined, semantics opaque (R4)
  Angle = 315
  AnglePitch = 0
  AngleRoll = 0
  Disabled = false
  Group = -> [ElementLink060,ElementLink061]
  LockAngle = true
  Multiply = false
  _ConstraintType = 36
  _LinkVersion = 1
  _Parent = -> Constraints
FEATURE [App::FeaturePython] ElementLink060  label="_Element065"  # link proxy (typed FeaturePython)
  LinkTransform = true
  LinkedObject = -> _Element065
  _LinkVersion = 1
  _Parent = -> Constraint030
FEATURE [Part::FeaturePython] _Element065  # link proxy (typed FeaturePython)
  Detach = false
  LinkTransform = true
  LinkedObject = -> Link021 [Chamfer001.Face20]
  _LinkVersion = 1
  _Parent = -> Elements
FEATURE [App::FeaturePython] ElementLink061  label="_Element066"  # link proxy (typed FeaturePython)
  LinkTransform = true
  LinkedObject = -> _Element066
  _LinkVersion = 1
  _Parent = -> Constraint030
FEATURE [Part::FeaturePython] _Element066  # link proxy (typed FeaturePython)
  Detach = false
  LinkTransform = true
  LinkedObject = -> Link007 [Pocket.Face7]
  _LinkVersion = 1
  _Parent = -> Elements
FEATURE [App::FeaturePython] Constraint031  label="PointInPlane008"  # WARN: FeaturePython — macro-defined, semantics opaque (R4)
  Disabled = false
  Group = -> [ElementLink062,ElementLink063]
  _ConstraintType = 3
  _LinkVersion = 1
  _Parent = -> Constraints
FEATURE [App::FeaturePython] ElementLink062  label="_Element067"  # link proxy (typed FeaturePython)
  LinkTransform = true
  LinkedObject = -> _Element067
  _LinkVersion = 1
  _Parent = -> Constraint031
FEATURE [Part::FeaturePython] _Element067  # link proxy (typed FeaturePython)
  Detach = false
  LinkTransform = true
  LinkedObject = -> Link021 [Chamfer001.Vertex27]
  _LinkVersion = 1
  _Parent = -> Elements
FEATURE [App::FeaturePython] ElementLink063  label="Element030"  # link proxy (typed FeaturePython)
  LinkTransform = true
  LinkedObject = -> Element030
  _LinkVersion = 1
  _Parent = -> Constraint031
FEATURE [App::FeaturePython] Constraint032  label="AxialAlignment005"  # WARN: FeaturePython — macro-defined, semantics opaque (R4)
  Angle = -135
  AnglePitch = 0
  AngleRoll = 0
  Disabled = false
  Group = -> [ElementLink064,ElementLink065]
  LockAngle = true
  Multiply = false
  _ConstraintType = 36
  _LinkVersion = 1
  _Parent = -> Constraints
FEATURE [App::FeaturePython] ElementLink064  label="_Element068"  # link proxy (typed FeaturePython)
  LinkTransform = true
  LinkedObject = -> _Element068
  _LinkVersion = 1
  _Parent = -> Constraint032
FEATURE [Part::FeaturePython] _Element068  # link proxy (typed FeaturePython)
  Detach = false
  LinkTransform = true
  LinkedObject = -> Link022 [Chamfer001.Face20]
  _LinkVersion = 1
  _Parent = -> Elements
FEATURE [App::FeaturePython] ElementLink065  label="Element017"  # link proxy (typed FeaturePython)
  LinkTransform = true
  LinkedObject = -> Element017
  _LinkVersion = 1
  _Parent = -> Constraint032
FEATURE [App::FeaturePython] Constraint033  label="PointInPlane009"  # WARN: FeaturePython — macro-defined, semantics opaque (R4)
  Disabled = false
  Group = -> [ElementLink066,ElementLink067]
  _ConstraintType = 3
  _LinkVersion = 1
  _Parent = -> Constraints
FEATURE [App::FeaturePython] ElementLink066  label="_Element069"  # link proxy (typed FeaturePython)
  LinkTransform = true
  LinkedObject = -> _Element069
  _LinkVersion = 1
  _Parent = -> Constraint033
FEATURE [Part::FeaturePython] _Element069  # link proxy (typed FeaturePython)
  Detach = false
  LinkTransform = true
  LinkedObject = -> Link022 [Chamfer001.Vertex27]
  _LinkVersion = 1
  _Parent = -> Elements
FEATURE [App::FeaturePython] ElementLink067  label="Element019"  # link proxy (typed FeaturePython)
  LinkTransform = true
  LinkedObject = -> Element019
  _LinkVersion = 1
  _Parent = -> Constraint033
FEATURE [App::FeaturePython] Constraint034  label="AxialAlignment006"  # WARN: FeaturePython — macro-defined, semantics opaque (R4)
  Angle = -45
  AnglePitch = 0
  AngleRoll = 0
  Disabled = false
  Group = -> [ElementLink068,ElementLink069]
  LockAngle = true
  Multiply = false
  _ConstraintType = 36
  _LinkVersion = 1
  _Parent = -> Constraints
FEATURE [App::FeaturePython] ElementLink068  label="_Element070"  # link proxy (typed FeaturePython)
  LinkTransform = true
  LinkedObject = -> _Element070
  _LinkVersion = 1
  _Parent = -> Constraint034
FEATURE [Part::FeaturePython] _Element070  # link proxy (typed FeaturePython)
  Detach = false
  LinkTransform = true
  LinkedObject = -> Link023 [Chamfer001.Face20]
  _LinkVersion = 1
  _Parent = -> Elements
FEATURE [App::FeaturePython] ElementLink069  label="_Element071"  # link proxy (typed FeaturePython)
  LinkTransform = true
  LinkedObject = -> _Element071
  _LinkVersion = 1
  _Parent = -> Constraint034
FEATURE [Part::FeaturePython] _Element071  # link proxy (typed FeaturePython)
  Detach = false
  LinkTransform = true
  LinkedObject = -> Link005 [Pocket.Face7]
  _LinkVersion = 1
  _Parent = -> Elements
FEATURE [App::FeaturePython] Constraint035  label="PointInPlane010"  # WARN: FeaturePython — macro-defined, semantics opaque (R4)
  Disabled = false
  Group = -> [ElementLink070,ElementLink071]
  _ConstraintType = 3
  _LinkVersion = 1
  _Parent = -> Constraints
FEATURE [App::FeaturePython] ElementLink070  label="_Element072"  # link proxy (typed FeaturePython)
  LinkTransform = true
  LinkedObject = -> _Element072
  _LinkVersion = 1
  _Parent = -> Constraint035
FEATURE [Part::FeaturePython] _Element072  # link proxy (typed FeaturePython)
  Detach = false
  LinkTransform = true
  LinkedObject = -> Link023 [Chamfer001.Vertex27]
  _LinkVersion = 1
  _Parent = -> Elements
FEATURE [App::FeaturePython] ElementLink071  label="Element019"  # link proxy (typed FeaturePython)
  LinkTransform = true
  LinkedObject = -> Element019
  _LinkVersion = 1
  _Parent = -> Constraint035
FEATURE [App::FeaturePython] Constraint036  label="AxialAlignment007"  # WARN: FeaturePython — macro-defined, semantics opaque (R4)
  Angle = 0
  AnglePitch = 0
  AngleRoll = 0
  Disabled = false
  Group = -> [ElementLink072,ElementLink073]
  LockAngle = false
  Multiply = false
  _ConstraintType = 36
  _LinkVersion = 1
  _Parent = -> Constraints
FEATURE [App::FeaturePython] ElementLink072  label="_Element073"  # link proxy (typed FeaturePython)
  LinkTransform = true
  LinkedObject = -> _Element073
  _LinkVersion = 1
  _Parent = -> Constraint036
FEATURE [Part::FeaturePython] _Element073  # link proxy (typed FeaturePython)
  Detach = false
  LinkTransform = true
  LinkedObject = -> Link024 [1.$Element.]
  _LinkVersion = 1
  _Parent = -> Elements
FEATURE [App::FeaturePython] ElementLink073  label="_Element074"  # link proxy (typed FeaturePython)
  LinkTransform = true
  LinkedObject = -> _Element074
  _LinkVersion = 1
  _Parent = -> Constraint036
FEATURE [Part::FeaturePython] _Element074  # link proxy (typed FeaturePython)
  Detach = false
  LinkTransform = true
  LinkedObject = -> Link020 [Chamfer001.Face13]
  _LinkVersion = 1
  _Parent = -> Elements
FEATURE [App::FeaturePython] Constraint037  label="PointInPlane011"  # WARN: FeaturePython — macro-defined, semantics opaque (R4)
  Disabled = false
  Group = -> [ElementLink074,ElementLink075]
  _ConstraintType = 3
  _LinkVersion = 1
  _Parent = -> Constraints
FEATURE [App::FeaturePython] ElementLink074  label="_Element075"  # link proxy (typed FeaturePython)
  LinkTransform = true
  LinkedObject = -> _Element075
  _LinkVersion = 1
  _Parent = -> Constraint037
FEATURE [Part::FeaturePython] _Element075  # link proxy (typed FeaturePython)
  Detach = false
  LinkTransform = true
  LinkedObject = -> Link024 [1.$Element001.]
  _LinkVersion = 1
  _Parent = -> Elements
FEATURE [App::FeaturePython] ElementLink075  label="_Element076"  # link proxy (typed FeaturePython)
  LinkTransform = true
  LinkedObject = -> _Element076
  _LinkVersion = 1
  _Parent = -> Constraint037
FEATURE [Part::FeaturePython] _Element076  # link proxy (typed FeaturePython)
  Detach = false
  LinkTransform = true
  LinkedObject = -> Link020 [Chamfer001.Face4]
  _LinkVersion = 1
  _Parent = -> Elements
FEATURE [App::FeaturePython] Constraint038  label="AxialAlignment008"  # WARN: FeaturePython — macro-defined, semantics opaque (R4)
  Angle = 0
  AnglePitch = 0
  AngleRoll = 0
  Disabled = false
  Group = -> [ElementLink076,ElementLink077]
  LockAngle = false
  Multiply = false
  _ConstraintType = 36
  _LinkVersion = 1
  _Parent = -> Constraints
FEATURE [App::FeaturePython] ElementLink076  label="_Element077"  # link proxy (typed FeaturePython)
  LinkTransform = true
  LinkedObject = -> _Element077
  _LinkVersion = 1
  _Parent = -> Constraint038
FEATURE [Part::FeaturePython] _Element077  # link proxy (typed FeaturePython)
  Detach = false
  LinkTransform = true
  LinkedObject = -> Link026 [1.$Element.]
  _LinkVersion = 1
  _Parent = -> Elements
FEATURE [App::FeaturePython] ElementLink077  label="_Element078"  # link proxy (typed FeaturePython)
  LinkTransform = true
  LinkedObject = -> _Element078
  _LinkVersion = 1
  _Parent = -> Constraint038
FEATURE [Part::FeaturePython] _Element078  # link proxy (typed FeaturePython)
  Detach = false
  LinkTransform = true
  LinkedObject = -> Link021 [Chamfer001.Face13]
  _LinkVersion = 1
  _Parent = -> Elements
FEATURE [App::FeaturePython] Constraint039  label="PointInPlane012"  # WARN: FeaturePython — macro-defined, semantics opaque (R4)
  Disabled = false
  Group = -> [ElementLink078,ElementLink079]
  _ConstraintType = 3
  _LinkVersion = 1
  _Parent = -> Constraints
FEATURE [App::FeaturePython] ElementLink078  label="_Element079"  # link proxy (typed FeaturePython)
  LinkTransform = true
  LinkedObject = -> _Element079
  _LinkVersion = 1
  _Parent = -> Constraint039
FEATURE [Part::FeaturePython] _Element079  # link proxy (typed FeaturePython)
  Detach = false
  LinkTransform = true
  LinkedObject = -> Link026 [1.$Element001.]
  _LinkVersion = 1
  _Parent = -> Elements
FEATURE [App::FeaturePython] ElementLink079  label="_Element080"  # link proxy (typed FeaturePython)
  LinkTransform = true
  LinkedObject = -> _Element080
  _LinkVersion = 1
  _Parent = -> Constraint039
FEATURE [Part::FeaturePython] _Element080  # link proxy (typed FeaturePython)
  Detach = false
  LinkTransform = true
  LinkedObject = -> Link021 [Chamfer001.Face4]
  _LinkVersion = 1
  _Parent = -> Elements
FEATURE [App::FeaturePython] Constraint040  label="AxialAlignment009"  # WARN: FeaturePython — macro-defined, semantics opaque (R4)
  Angle = 0
  AnglePitch = 0
  AngleRoll = 0
  Disabled = false
  Group = -> [ElementLink080,ElementLink081]
  LockAngle = false
  Multiply = false
  _ConstraintType = 36
  _LinkVersion = 1
  _Parent = -> Constraints
FEATURE [App::FeaturePython] ElementLink080  label="_Element081"  # link proxy (typed FeaturePython)
  LinkTransform = true
  LinkedObject = -> _Element081
  _LinkVersion = 1
  _Parent = -> Constraint040
FEATURE [Part::FeaturePython] _Element081  # link proxy (typed FeaturePython)
  Detach = false
  LinkTransform = true
  LinkedObject = -> Link027 [1.$Element.]
  _LinkVersion = 1
  _Parent = -> Elements
FEATURE [App::FeaturePython] ElementLink081  label="_Element082"  # link proxy (typed FeaturePython)
  LinkTransform = true
  LinkedObject = -> _Element082
  _LinkVersion = 1
  _Parent = -> Constraint040
FEATURE [Part::FeaturePython] _Element082  # link proxy (typed FeaturePython)
  Detach = false
  LinkTransform = true
  LinkedObject = -> Link022 [Chamfer001.Face13]
  _LinkVersion = 1
  _Parent = -> Elements
FEATURE [App::FeaturePython] Constraint041  label="PointInPlane013"  # WARN: FeaturePython — macro-defined, semantics opaque (R4)
  Disabled = false
  Group = -> [ElementLink082,ElementLink083]
  _ConstraintType = 3
  _LinkVersion = 1
  _Parent = -> Constraints
FEATURE [App::FeaturePython] ElementLink082  label="_Element083"  # link proxy (typed FeaturePython)
  LinkTransform = true
  LinkedObject = -> _Element083
  _LinkVersion = 1
  _Parent = -> Constraint041
FEATURE [Part::FeaturePython] _Element083  # link proxy (typed FeaturePython)
  Detach = false
  LinkTransform = true
  LinkedObject = -> Link027 [1.$Element001.]
  _LinkVersion = 1
  _Parent = -> Elements
FEATURE [App::FeaturePython] ElementLink083  label="_Element084"  # link proxy (typed FeaturePython)
  LinkTransform = true
  LinkedObject = -> _Element084
  _LinkVersion = 1
  _Parent = -> Constraint041
FEATURE [Part::FeaturePython] _Element084  # link proxy (typed FeaturePython)
  Detach = false
  LinkTransform = true
  LinkedObject = -> Link022 [Chamfer001.Face4]
  _LinkVersion = 1
  _Parent = -> Elements
FEATURE [App::FeaturePython] Constraint042  label="AxialAlignment010"  # WARN: FeaturePython — macro-defined, semantics opaque (R4)
  Angle = 0
  AnglePitch = 0
  AngleRoll = 0
  Disabled = false
  Group = -> [ElementLink084,ElementLink085]
  LockAngle = false
  Multiply = false
  _ConstraintType = 36
  _LinkVersion = 1
  _Parent = -> Constraints
FEATURE [App::FeaturePython] ElementLink084  label="_Element085"  # link proxy (typed FeaturePython)
  LinkTransform = true
  LinkedObject = -> _Element085
  _LinkVersion = 1
  _Parent = -> Constraint042
FEATURE [Part::FeaturePython] _Element085  # link proxy (typed FeaturePython)
  Detach = false
  LinkTransform = true
  LinkedObject = -> Link028 [1.$Element.]
  _LinkVersion = 1
  _Parent = -> Elements
FEATURE [App::FeaturePython] ElementLink085  label="_Element086"  # link proxy (typed FeaturePython)
  LinkTransform = true
  LinkedObject = -> _Element086
  _LinkVersion = 1
  _Parent = -> Constraint042
FEATURE [Part::FeaturePython] _Element086  # link proxy (typed FeaturePython)
  Detach = false
  LinkTransform = true
  LinkedObject = -> Link023 [Chamfer001.Face13]
  _LinkVersion = 1
  _Parent = -> Elements
FEATURE [App::FeaturePython] Constraint043  label="PointInPlane014"  # WARN: FeaturePython — macro-defined, semantics opaque (R4)
  Disabled = false
  Group = -> [ElementLink086,ElementLink087]
  _ConstraintType = 3
  _LinkVersion = 1
  _Parent = -> Constraints
FEATURE [App::FeaturePython] ElementLink086  label="_Element087"  # link proxy (typed FeaturePython)
  LinkTransform = true
  LinkedObject = -> _Element087
  _LinkVersion = 1
  _Parent = -> Constraint043
FEATURE [Part::FeaturePython] _Element087  # link proxy (typed FeaturePython)
  Detach = false
  LinkTransform = true
  LinkedObject = -> Link028 [1.$Element001.]
  _LinkVersion = 1
  _Parent = -> Elements
FEATURE [App::FeaturePython] ElementLink087  label="_Element088"  # link proxy (typed FeaturePython)
  LinkTransform = true
  LinkedObject = -> _Element088
  _LinkVersion = 1
  _Parent = -> Constraint043
FEATURE [Part::FeaturePython] _Element088  # link proxy (typed FeaturePython)
  Detach = false
  LinkTransform = true
  LinkedObject = -> Link023 [Chamfer001.Face4]
  _LinkVersion = 1
  _Parent = -> Elements
FEATURE [App::FeaturePython] Constraint044  label="PlaneAlignment005"  # WARN: FeaturePython — macro-defined, semantics opaque (R4)
  Angle = 0
  AnglePitch = 0
  AngleRoll = 0
  Cascade = false
  Disabled = false
  Group = -> [ElementLink088,ElementLink089]
  LockAngle = false
  _ConstraintType = 37
  _LinkVersion = 1
  _Parent = -> Constraints
FEATURE [App::FeaturePython] ElementLink088  label="_Element089"  # link proxy (typed FeaturePython)
  LinkTransform = true
  LinkedObject = -> _Element089
  _LinkVersion = 1
  _Parent = -> Constraint044
FEATURE [Part::FeaturePython] _Element089  # link proxy (typed FeaturePython)
  Detach = false
  LinkTransform = true
  LinkedObject = -> Link016 [1.$Element.]
  _LinkVersion = 1
  _Parent = -> Elements
FEATURE [App::FeaturePython] ElementLink089  label="_Element033"  # link proxy (typed FeaturePython)
  LinkTransform = true
  LinkedObject = -> _Element033
  _LinkVersion = 1
  _Parent = -> Constraint044
FEATURE [Part::FeaturePython] _Element090  # link proxy (typed FeaturePython)
  Detach = false
  LinkTransform = true
  LinkedObject = -> Link016 [1.$Element001.]
  _LinkVersion = 1
  _Parent = -> Elements
FEATURE [App::FeaturePython] Constraint045  label="AxialAlignment011"  # WARN: FeaturePython — macro-defined, semantics opaque (R4)
  Angle = 0
  AnglePitch = 0
  AngleRoll = 0
  Disabled = false
  Group = -> [ElementLink090,ElementLink091]
  LockAngle = false
  Multiply = false
  _ConstraintType = 36
  _LinkVersion = 1
  _Parent = -> Constraints
FEATURE [App::FeaturePython] ElementLink090  label="_Element015"  # link proxy (typed FeaturePython)
  LinkTransform = true
  LinkedObject = -> _Element015
  _LinkVersion = 1
  _Parent = -> Constraint045
FEATURE [App::FeaturePython] ElementLink091  label="_Element091"  # link proxy (typed FeaturePython)
  LinkTransform = true
  LinkedObject = -> _Element091
  _LinkVersion = 1
  _Parent = -> Constraint045
FEATURE [Part::FeaturePython] _Element091  # link proxy (typed FeaturePython)
  Detach = false
  LinkTransform = true
  LinkedObject = -> Link010 [Fillet.Face9]
  _LinkVersion = 1
  _Parent = -> Elements
FEATURE [App::FeaturePython] Constraint046  label="PointInPlane015"  # WARN: FeaturePython — macro-defined, semantics opaque (R4)
  Disabled = false
  Group = -> [ElementLink092,ElementLink093]
  _ConstraintType = 3
  _LinkVersion = 1
  _Parent = -> Constraints
FEATURE [App::FeaturePython] ElementLink092  label="_Element092"  # link proxy (typed FeaturePython)
  LinkTransform = true
  LinkedObject = -> _Element092
  _LinkVersion = 1
  _Parent = -> Constraint046
FEATURE [Part::FeaturePython] _Element092  # link proxy (typed FeaturePython)
  Detach = false
  LinkTransform = true
  LinkedObject = -> Link011 [Chamfer001.Vertex3]
  _LinkVersion = 1
  _Parent = -> Elements
FEATURE [App::FeaturePython] ElementLink093  label="_Element093"  # link proxy (typed FeaturePython)
  LinkTransform = true
  LinkedObject = -> _Element093
  _LinkVersion = 1
  _Parent = -> Constraint046
FEATURE [Part::FeaturePython] _Element093  # link proxy (typed FeaturePython)
  Detach = false
  LinkTransform = true
  LinkedObject = -> Link010 [Fillet.Face38]
  _LinkVersion = 1
  _Parent = -> Elements
FEATURE [App::FeaturePython] Constraint047  label="SameOrientation"  # WARN: FeaturePython — macro-defined, semantics opaque (R4)
  Disabled = false
  Group = -> [ElementLink094,ElementLink095]
  _ConstraintType = 2
  _LinkVersion = 1
  _Parent = -> Constraints
FEATURE [App::FeaturePython] ElementLink094  label="_Element094"  # link proxy (typed FeaturePython)
  LinkTransform = true
  LinkedObject = -> _Element094
  _LinkVersion = 1
  _Parent = -> Constraint047
FEATURE [Part::FeaturePython] _Element094  # link proxy (typed FeaturePython)
  Detach = false
  LinkTransform = true
  LinkedObject = -> Link011 [Chamfer001.Face2]
  _LinkVersion = 1
  _Parent = -> Elements
FEATURE [App::FeaturePython] ElementLink095  label="_Element095"  # link proxy (typed FeaturePython)
  LinkTransform = true
  LinkedObject = -> _Element095
  _LinkVersion = 1
  _Parent = -> Constraint047
FEATURE [Part::FeaturePython] _Element095  # link proxy (typed FeaturePython)
  Detach = false
  LinkTransform = true
  LinkedObject = -> Link010 [Fillet.Face4]
  _LinkVersion = 1
  _Parent = -> Elements
FEATURE [Part::FeaturePython] _Element096  # link proxy (typed FeaturePython)
  Detach = false
  LinkTransform = true
  LinkedObject = -> Link010 [Fillet.Face2]
  _LinkVersion = 1
  _Parent = -> Elements

RESOLVED EXTERNAL PARTS (link-assembly join: the EXTERNAL_REF files above that resolve inside this repo's crawl, each included once):
---- part dystans-lozyska.FCStd = doc fcstd_e622bdcf3388 ----
FCSTD DOCUMENT  (FreeCAD 2020.10.16R22739 +2665 (Git))
Label: dystans-lozyska
License: All rights reserved
LicenseURL: http://en.wikipedia.org/wiki/All_rights_reserved
objects: Sketcher::SketchObject×3, PartDesign::Pad×2, PartDesign::Fillet×2, PartDesign::Chamfer×2, PartDesign::Pocket×1, PartDesign::Body×1
note: 25 computed .brp shape members not serialized (recipe doc carries the construction recipe); baked Part::Feature solids carry a one-line shape summary decoded from their .brp

FEATURE [Sketcher::SketchObject] Sketch
  MapMode = 5
  Support = -> [XY_Plane]
  sketch-geometry (1):
    g0: Circle CenterX=0 CenterY=0 CenterZ=0 NormalX=0 NormalY=0 NormalZ=1 AngleXU=0 Radius=8
  constraints (2):
    c: Coincident(g0,g-1)
    c: Diameter(g0) = 16
FEATURE [PartDesign::Pad] Pad
  ClaimChildren = false
  Direction = (1,1,1)
  Length = 4
  Length2 = 100
  NewSolid = false
  Profile = -> Sketch
  Suppress = false
  Type = 0
FEATURE [Sketcher::SketchObject] Sketch001
  MapMode = 5
  Placement = pos=(0,0,4) rot=(0,0,1;0rad)
  Support = -> [Pad]
  sketch-geometry (1):
    g0: Circle CenterX=0 CenterY=0 CenterZ=0 NormalX=0 NormalY=0 NormalZ=1 AngleXU=0 Radius=4
  constraints (2):
    c: Coincident(g0,g-1)
    c: Diameter(g0) = 8
FEATURE [PartDesign::Pad] Pad001
  BaseFeature = -> Pad
  ClaimChildren = false
  Direction = (1,1,1)
  Length = 7
  Length2 = 100
  NewSolid = false
  Profile = -> Sketch001
  Suppress = false
  Type = 0
FEATURE [Sketcher::SketchObject] Sketch002
  MapMode = 5
  Placement = pos=(0,0,11) rot=(0,0,1;0rad)
  Support = -> [Pad001]
  sketch-geometry (4):
    g0: ArcOfCircle CenterX=0 CenterY=0 CenterZ=0 NormalX=0 NormalY=0 NormalZ=1 AngleXU=0 Radius=4.05 StartAngle=5.44901 EndAngle=7.11736
    g1: LineSegment StartX=1 StartY=3 StartZ=0 EndX=2.72075 EndY=3 EndZ=0
    g2: LineSegment StartX=1 StartY=-3 StartZ=0 EndX=2.72075 EndY=-3 EndZ=0
    g3: ArcOfCircle CenterX=1 CenterY=0 CenterZ=0 NormalX=0 NormalY=0 NormalZ=1 AngleXU=0 Radius=3 StartAngle=1.5708 EndAngle=4.71239
  constraints (11):
    c: Coincident(g0,g-1)
    c: Diameter(g0) = 8.1
    c: Horizontal(g2)
    c: Horizontal(g1)
    c: Coincident(g0,g2)
    c: Coincident(g0,g1)
    c: PointOnObject(g3,g-1)
    c: DistanceX(g3) = 1
    c: Tangent(g3,g1) = 1.5708
    c: Tangent(g3,g2) = -1.5708
    c: Diameter(g3) = 6
FEATURE [PartDesign::Pocket] Pocket
  BaseFeature = -> Pad001
  ClaimChildren = false
  Length = 5
  Length2 = 100
  NewSolid = false
  Profile = -> Sketch002
  Suppress = false
  Type = 1
FEATURE [PartDesign::Fillet] Fillet
  Base = -> Pocket [Edge15,Edge20]
  BaseFeature = -> Pocket
  NewSolid = false
  Radius = 0.3
  SupportTransform = true
  Suppress = false
FEATURE [PartDesign::Fillet] Fillet001
  Base = -> Fillet [Edge20,Edge24]
  BaseFeature = -> Fillet
  NewSolid = false
  Radius = 2
  SupportTransform = true
  Suppress = false
FEATURE [PartDesign::Chamfer] Chamfer
  Angle = 5
  Base = -> Fillet001 [Edge9]
  BaseFeature = -> Fillet001
  ChamferType = 2
  FlipDirection = false
  NewSolid = false
  Size = 3
  Size2 = 1
  SupportTransform = true
  Suppress = false
FEATURE [PartDesign::Chamfer] Chamfer001
  Angle = 45
  Base = -> Chamfer [Edge34,Edge14,Edge18,Edge22,Edge26,Edge29]
  BaseFeature = -> Chamfer
  ChamferType = 1
  FlipDirection = false
  NewSolid = false
  Size = 0.5
  Size2 = 1
  SupportTransform = true
  Suppress = false
FEATURE [PartDesign::Body] Body  label="dystans-lozyska"
  ExportMode = 0
  Group = -> [Sketch,Pad,Sketch001,Pad001,Sketch002,Pocket,Fillet,Fillet001,Chamfer,Chamfer001]
  Origin = -> Origin
  Tip = -> Chamfer001
  _ExportChildren = -> [Pad,Pad001,Pocket,Fillet,Fillet001,Chamfer,Chamfer001]
  _GroupVersion = 1
---- part kolkozebmodul1fi5sc.FCStd = doc fcstd_7b8e23e37805 ----
FCSTD DOCUMENT  (FreeCAD 2020.10.16R22739 +2665 (Git))
Label: kolkozebmodul1fi5sc
License: All rights reserved
objects: Sketcher::SketchObject×2, Part::FeaturePython×1, PartDesign::FeatureBase×1, PartDesign::Pocket×1, PartDesign::Groove×1, PartDesign::Body×1
note: 12 computed .brp shape members not serialized (recipe doc carries the construction recipe); baked Part::Feature solids carry a one-line shape summary decoded from their .brp

FEATURE [Part::FeaturePython] involutegear  # WARN: FeaturePython — macro-defined, semantics opaque (R4)
  backlash = 0
  beta = 0
  clearance = 0.25
  double_helix = false
  dw = 12
  head = 0
  height = 55
  module = 1
  numpoints = 6
  pressure_angle = 20
  properties_from_tool = true
  reversed_backlash = false
  shift = 0
  simple = false
  teeth = 12
  transverse_pitch = 3.14159
  undercut = true
FEATURE [PartDesign::FeatureBase] BaseFeature
  BaseFeature = -> involutegear
  NewSolid = false
  Suppress = false
FEATURE [Sketcher::SketchObject] Sketch
  MapMode = 5
  Placement = pos=(0,0,55) rot=(0,0,1;0rad)
  Support = -> [BaseFeature]
  sketch-geometry (2):
    g0: ArcOfCircle CenterX=0 CenterY=0 CenterZ=0 NormalX=0 NormalY=0 NormalZ=1 AngleXU=0 Radius=2.5 StartAngle=0.643501 EndAngle=5.63968
    g1: LineSegment StartX=2 StartY=1.5 StartZ=0 EndX=2 EndY=-1.5 EndZ=0
  constraints (6):
    c: Coincident(g0,g-1)
    c: Diameter(g0) = 5
    c: Vertical(g1)
    c: Coincident(g0,g1)
    c: Coincident(g0,g1)
    c: DistanceX(g0) = 2
FEATURE [PartDesign::Pocket] Pocket
  BaseFeature = -> BaseFeature
  ClaimChildren = false
  Length = 25
  Length2 = 100
  NewSolid = false
  Profile = -> Sketch
  Suppress = false
  Type = 0
FEATURE [Sketcher::SketchObject] Sketch001
  ExternalGeometry = -> [Pocket]
  MapMode = 5
  Placement = pos=(0,0,0) rot=(1,0,0;1.5708rad)
  Support = -> [XZ_Plane]
  sketch-geometry (4):
    g0: LineSegment StartX=4.5 StartY=36.4434 StartZ=0 EndX=4.5 EndY=55 EndZ=0
    g1: LineSegment StartX=4.5 StartY=55 StartZ=0 EndX=7 EndY=55 EndZ=0
    g2: LineSegment StartX=7 StartY=55 StartZ=0 EndX=7 EndY=35 EndZ=0
    g3: LineSegment StartX=7 StartY=35 StartZ=0 EndX=4.5 EndY=36.4434 EndZ=0
  constraints (12):
    c: Vertical(g0)
    c: Coincident(g0,g1)
    c: Coincident(g1,g2)
    c: Vertical(g2)
    c: Coincident(g2,g3)
    c: Coincident(g3,g0)
    c: DistanceX(g0) = 4.5
    c: DistanceX(g2) = 7
    c: DistanceY(g2,g2) = 20
    c: Horizontal(g1)
    c: Horizontal(g1,g-3)
    c: Angle(g2,g3) = 1.0472
FEATURE [PartDesign::Groove] Groove
  Angle = 360
  Axis = (0,-2e-16,1)
  Base = (0,0,0)
  BaseFeature = -> Pocket
  ClaimChildren = false
  NewSolid = false
  Profile = -> Sketch001
  ReferenceAxis = -> Sketch001 [V_Axis]
  Suppress = false
FEATURE [PartDesign::Body] Body  label="kolkozebstoz"
  BaseFeature = -> involutegear
  ExportMode = 0
  Group = -> [BaseFeature,Sketch,Pocket,Sketch001,Groove]
  Origin = -> Origin
  Tip = -> Groove
  _ExportChildren = -> [BaseFeature,Pocket,Groove]
  _GroupVersion = 1
---- part krokowiec-dol.FCStd = doc fcstd_74b018722f62 ----
FCSTD DOCUMENT  (FreeCAD 2020.12.13R23076 +3015 (Git))
Label: krokowiec-dol
License: All rights reserved
objects: Sketcher::SketchObject×7, PartDesign::Pocket×4, PartDesign::Pad×2, PartDesign::LinearPattern×2, TechDraw::DrawProjGroupItem×2, TechDraw::DrawViewDimension×2, TechDraw::DrawSVGTemplate×1, PartDesign::MultiTransform×1, PartDesign::Fillet×1, PartDesign::Body×1, TechDraw::DrawProjGroup×1, TechDraw::DrawPage×1
note: 35 computed .brp shape members not serialized (recipe doc carries the construction recipe); baked Part::Feature solids carry a one-line shape summary decoded from their .brp

FEATURE [Sketcher::SketchObject] Sketch
  MapMode = 5
  Support = -> [XY_Plane]
  sketch-geometry (5):
    g0: LineSegment StartX=25 StartY=25 StartZ=0 EndX=-25 EndY=25 EndZ=0
    g1: LineSegment StartX=-25 StartY=-25 StartZ=0 EndX=25 EndY=-25 EndZ=0
    g2: Circle [constr] CenterX=0 CenterY=0 CenterZ=0 NormalX=0 NormalY=0 NormalZ=1 AngleXU=0 Radius=35.3553
    g3: LineSegment StartX=-25 StartY=25 StartZ=0 EndX=-25 EndY=-25 EndZ=0
    g4: LineSegment StartX=25 StartY=25 StartZ=0 EndX=25 EndY=-25 EndZ=0
  constraints (14):
    c: Equal(g0,g1)
    c: PointOnObject(g0,g2)
    c: PointOnObject(g1,g2)
    c: PointOnObject(g1,g2)
    c: PointOnObject(g0,g2)
    c: Coincident(g2,g-1)
    c: Horizontal(g0)
    c: DistanceX(g0,g0) = 50
    c: DistanceY(g1,g0) = 50
    c: Horizontal(g1)
    c: Coincident(g0,g3)
    c: Coincident(g3,g1)
    c: Coincident(g0,g4)
    c: Coincident(g4,g1)
FEATURE [PartDesign::Pad] Pad
  ClaimChildren = false
  Direction = (1,1,1)
  Fit = 0
  FitJoin = 0
  InnerFit = 0
  InnerFitJoin = 0
  InnerTaperAngle = 0
  InnerTaperAngleRev = 0
  Length = 10
  Length2 = 100
  NewSolid = false
  Profile = -> Sketch
  Suppress = false
  Type = 0
FEATURE [Sketcher::SketchObject] Sketch001
  MapMode = 5
  Placement = pos=(0,0,10) rot=(0,0,1;0rad)
  Support = -> [Pad]
  sketch-geometry (5):
    g0: LineSegment StartX=21 StartY=21 StartZ=0 EndX=-21 EndY=21 EndZ=0
    g1: LineSegment StartX=-21 StartY=21 StartZ=0 EndX=-21 EndY=-21 EndZ=0
    g2: LineSegment StartX=-21 StartY=-21 StartZ=0 EndX=21 EndY=-21 EndZ=0
    g3: LineSegment StartX=21 StartY=-21 StartZ=0 EndX=21 EndY=21 EndZ=0
    g4: Circle [constr] CenterX=0 CenterY=0 CenterZ=0 NormalX=0 NormalY=0 NormalZ=1 AngleXU=0 Radius=29.6985
  constraints (14):
    c: Coincident(g0,g1)
    c: Coincident(g1,g2)
    c: Coincident(g2,g3)
    c: Coincident(g3,g0)
    c: Equal(g0,g1)
    c: Equal(g0,g2)
    c: Equal(g0,g3)
    c: PointOnObject(g0,g4)
    c: PointOnObject(g1,g4)
    c: PointOnObject(g2,g4)
    c: PointOnObject(g3,g4)
    c: Coincident(g4,g-1)
    c: DistanceX(g0,g0) = 42
    c: Horizontal(g0)
FEATURE [PartDesign::Pocket] Pocket
  BaseFeature = -> Pad
  ClaimChildren = false
  Fit = 0
  FitJoin = 0
  InnerFit = 0
  InnerFitJoin = 0
  InnerTaperAngle = 0
  InnerTaperAngleRev = 0
  Length = 7
  Length2 = 100
  NewSolid = false
  Profile = -> Sketch001
  Suppress = false
  Type = 0
FEATURE [Sketcher::SketchObject] Sketch002
  MapMode = 5
  Placement = pos=(0,0,3) rot=(0,0,1;0rad)
  Support = -> [Pocket]
  sketch-geometry (1):
    g0: Circle CenterX=0 CenterY=0 CenterZ=0 NormalX=0 NormalY=0 NormalZ=1 AngleXU=0 Radius=11
  constraints (2):
    c: Coincident(g0,g-1)
    c: Diameter(g0) = 22
FEATURE [PartDesign::Pocket] Pocket001
  BaseFeature = -> Pocket
  ClaimChildren = false
  Fit = 0
  FitJoin = 0
  InnerFit = 0
  InnerFitJoin = 0
  InnerTaperAngle = 0
  InnerTaperAngleRev = 0
  Length = 5
  Length2 = 100
  NewSolid = false
  Profile = -> Sketch002
  Suppress = false
  Type = 1
FEATURE [Sketcher::SketchObject] Sketch005
  MapMode = 5
  Placement = pos=(0,0,5) rot=(0,0,1;0rad)
  sketch-geometry (4):
    g0: Circle CenterX=-15.5 CenterY=15.5 CenterZ=0 NormalX=0 NormalY=0 NormalZ=1 AngleXU=0 Radius=2
    g1: Circle CenterX=15.5 CenterY=15.5 CenterZ=0 NormalX=0 NormalY=0 NormalZ=1 AngleXU=0 Radius=2
    g2: Circle CenterX=15.5 CenterY=-15.5 CenterZ=0 NormalX=0 NormalY=0 NormalZ=1 AngleXU=0 Radius=2
    g3: Circle CenterX=-15.5 CenterY=-15.5 CenterZ=0 NormalX=0 NormalY=0 NormalZ=1 AngleXU=0 Radius=2
  constraints (9):
    c: Symmetric(g3,g0,g-1)
    c: Symmetric(g0,g1,g-2)
    c: Symmetric(g2,g1,g-1)
    c: Equal(g3,g2)
    c: Equal(g2,g1)
    c: Equal(g1,g0)
    c: DistanceX(g0,g1) = 31
    c: DistanceY(g2,g1) = 31
    c: Diameter(g1) = 4
FEATURE [PartDesign::Pocket] Pocket004
  BaseFeature = -> Pocket001
  ClaimChildren = false
  Fit = 0
  FitJoin = 0
  InnerFit = 0
  InnerFitJoin = 0
  InnerTaperAngle = 0
  InnerTaperAngleRev = 0
  Length = 5
  Length2 = 100
  NewSolid = false
  Profile = -> Sketch005
  Suppress = false
  Type = 0
FEATURE [Sketcher::SketchObject] Sketch007
  MapMode = 5
  Support = -> [XY_Plane]
  sketch-geometry (4):
    g0: ArcOfCircle CenterX=-28 CenterY=15 CenterZ=0 NormalX=0 NormalY=0 NormalZ=1 AngleXU=0 Radius=2 StartAngle=3.14159 EndAngle=6.28319
    g1: ArcOfCircle CenterX=-28 CenterY=25 CenterZ=0 NormalX=0 NormalY=0 NormalZ=1 AngleXU=0 Radius=2 StartAngle=0 EndAngle=3.14159
    g2: LineSegment StartX=-26 StartY=15 StartZ=0 EndX=-26 EndY=25 EndZ=0
    g3: LineSegment StartX=-30 StartY=15 StartZ=0 EndX=-30 EndY=25 EndZ=0
  constraints (10):
    c: Tangent(g0,g3) = 1.5708
    c: Tangent(g0,g2) = -1.5708
    c: Tangent(g2,g1) = -1.5708
    c: Tangent(g3,g1) = 1.5708
    c: Vertical(g2)
    c: Equal(g0,g1)
    c: Radius(g1) = 2
    c: DistanceY(g0,g1) = 10
    c: DistanceY(g0) = 15
    c: DistanceX(g0,g-1) = 28
FEATURE [PartDesign::LinearPattern] LinearPattern
  CopyShape = false
  Direction = -> Sketch007 [H_Axis]
  Length = 56
  NewSolid = false
  Occurrences = 2
  SubTransform = true
  Suppress = false
FEATURE [PartDesign::LinearPattern] LinearPattern001
  CopyShape = false
  Direction = -> Sketch007 [V_Axis]
  Length = 18
  NewSolid = false
  Occurrences = 2
  SubTransform = true
  Suppress = false
FEATURE [TechDraw::DrawSVGTemplate] Template
  EditableTexts = Designed_by_Name=Designed by Name; Drawing_number=Drawing number; FC-Date=Date; FC-SC=Scale; FC-SH=Sheet; FC-Title=Title; Subtitle=Subtitle; Weight=Weight
  Height = 210
  Orientation = 1
  Width = 297
FEATURE [Sketcher::SketchObject] Sketch006
  ExternalGeometry = -> [Pocket004]
  MapMode = 5
  Support = -> [XY_Plane]
  sketch-geometry (8):
    g0: LineSegment StartX=-25 StartY=25 StartZ=0 EndX=25 EndY=25 EndZ=0
    g1: LineSegment StartX=35 StartY=-7.67949 StartZ=0 EndX=35 EndY=50 EndZ=0
    g2: LineSegment StartX=35 StartY=50 StartZ=0 EndX=-35 EndY=50 EndZ=0
    g3: LineSegment StartX=-35 StartY=50 StartZ=0 EndX=-35 EndY=-7.67949 EndZ=0
    g4: LineSegment StartX=-35 StartY=-7.67949 StartZ=0 EndX=-25 EndY=-25 EndZ=0
    g5: LineSegment StartX=-25 StartY=-25 StartZ=0 EndX=-25 EndY=25 EndZ=0
    g6: LineSegment StartX=35 StartY=-7.67949 StartZ=0 EndX=25 EndY=-25 EndZ=0
    g7: LineSegment StartX=25 StartY=-25 StartZ=0 EndX=25 EndY=25 EndZ=0
  constraints (19):
    c: Coincident(g-3,g0)
    c: Coincident(g0,g-3)
    c: Vertical(g1)
    c: Coincident(g1,g2)
    c: Coincident(g2,g3)
    c: Symmetric(g2,g1,g-2)
    c: Symmetric(g3,g1,g-2)
    c: DistanceX(g2,g2) = 70
    c: DistanceY(g1) = 50
    c: Coincident(g3,g4)
    c: Coincident(g4,g5)
    c: Coincident(g5,g0)
    c: Vertical(g5)
    c: Coincident(g1,g6)
    c: Coincident(g6,g7)
    c: Coincident(g7,g0)
    c: Symmetric(g6,g4,g-2)
    c: Angle(g1,g6) = 2.61799
    c: DistanceY(g6) = -25
FEATURE [PartDesign::Pad] Pad001
  BaseFeature = -> Pocket004
  ClaimChildren = false
  Direction = (1,1,1)
  Fit = 0
  FitJoin = 0
  InnerFit = 0
  InnerFitJoin = 0
  InnerTaperAngle = 0
  InnerTaperAngleRev = 0
  Length = 10
  Length2 = 100
  NewSolid = false
  Profile = -> Sketch006
  Suppress = false
  Type = 0
FEATURE [PartDesign::Pocket] Pocket005
  BaseFeature = -> Pad001
  ClaimChildren = false
  Fit = 0
  FitJoin = 0
  InnerFit = 0
  InnerFitJoin = 0
  InnerTaperAngle = 0
  InnerTaperAngleRev = 0
  Length = 5
  Length2 = 100
  NewSolid = false
  Profile = -> Sketch007
  Reversed = true
  Suppress = false
  Type = 1
FEATURE [PartDesign::MultiTransform] MultiTransform
  BaseFeature = -> Pocket005
  CopyShape = false
  NewSolid = false
  OriginalSubs = -> [Pocket005]
  Originals = -> [Pocket005]
  SubTransform = true
  Suppress = false
  Transformations = -> [LinearPattern,LinearPattern001]
FEATURE [PartDesign::Fillet] Fillet
  Base = -> MultiTransform [Edge48,Edge45,Edge31,Edge32,Edge44,Edge50]
  BaseFeature = -> MultiTransform
  NewSolid = false
  Radius = 5
  SupportTransform = true
  Suppress = false
FEATURE [Sketcher::SketchObject] Sketch008
  ExternalGeometry = -> [Fillet]
  MapMode = 5
  Support = -> [XY_Plane]
  sketch-geometry (3):
    g0: GeomPoint X=-28 Y=43 Z=0
    g1: GeomPoint X=28 Y=43 Z=0
    g2: LineSegment StartX=-28 StartY=43 StartZ=0 EndX=28 EndY=43 EndZ=0
  constraints (4):
    c: Coincident(g0,g-3)
    c: Coincident(g1,g-4)
    c: Coincident(g2,g0)
    c: Coincident(g2,g1)
FEATURE [PartDesign::Body] Body  label="krokowiec-dol"
  ExportMode = 0
  Group = -> [Sketch,Pad,Sketch001,Pocket,Sketch002,Pocket001,Sketch005,Pocket004,Sketch006,Pad001,Sketch007,Pocket005,MultiTransform,LinearPattern,LinearPattern001,Fillet,Sketch008]
  Origin = -> Origin
  Tip = -> Fillet
  _ExportChildren = -> [Pad,Pocket,Pocket001,Pocket004,Pad001,Pocket005,MultiTransform,LinearPattern,LinearPattern001,Fillet,Sketch008]
  _GroupVersion = 1
FEATURE [TechDraw::DrawProjGroupItem] ProjItem  label="Front"
  CoarseView = false
  Direction = (0,0,1)
  Focus = 100
  HardHidden = false
  IsoCount = 0
  IsoHidden = false
  IsoVisible = false
  LockPosition = true
  Perspective = false
  Rotation = 0
  RotationVector = (1,0,0)
  ScaleType = 2
  SeamHidden = false
  SeamVisible = true
  SmoothHidden = false
  SmoothVisible = true
  Source = -> [Fillet]
  Type = 0
  X = 0
  XDirection = (1,0,0)
  Y = 0
FEATURE [TechDraw::DrawProjGroupItem] ProjItem001  label="Bottom"
  CoarseView = false
  Direction = (0,-1,0)
  Focus = 100
  HardHidden = false
  IsoCount = 0
  IsoHidden = false
  IsoVisible = false
  LockPosition = false
  Perspective = false
  Rotation = 0
  RotationVector = (1,0,0)
  ScaleType = 2
  SeamHidden = false
  SeamVisible = true
  SmoothHidden = false
  SmoothVisible = true
  Source = -> [Fillet]
  Type = 5
  X = 0
  XDirection = (1,0,0)
  Y = 57.5
FEATURE [TechDraw::DrawProjGroup] ProjGroup
  Anchor = -> ProjItem
  AutoDistribute = true
  LockPosition = false
  ProjectionType = 0
  Rotation = 0
  ScaleType = 0
  Source = -> [Fillet]
  Views = -> [ProjItem,ProjItem001]
  X = 148.5
  Y = 105
  spacingX = 15
  spacingY = 15
FEATURE [TechDraw::DrawViewDimension] Dimension
  Arbitrary = false
  FormatSpec = %.2f
  Inverted = false
  LockPosition = false
  MeasureType = 1
  OverTolerance = 0
  References2D = -> [ProjItem]
  Rotation = 0
  ScaleType = 0
  TheoreticalExact = false
  Type = 1
  UnderTolerance = 0
  X = 0
  Y = -18.25
FEATURE [TechDraw::DrawViewDimension] Dimension001
  Arbitrary = false
  FormatSpec = ⌀%.2f
  Inverted = false
  LockPosition = false
  MeasureType = 1
  OverTolerance = 0
  References2D = -> [ProjItem]
  Rotation = 0
  ScaleType = 0
  TheoreticalExact = false
  Type = 5
  UnderTolerance = 0
  X = 54.5294
  Y = 6.58114
FEATURE [TechDraw::DrawPage] Page
  KeepUpdated = true
  NextBalloonIndex = 1
  ProjectionType = 0
  Template = -> Template
  Views = -> [ProjGroup,Dimension,Dimension001]
---- part krokowiec-nema17.FCStd = doc fcstd_135561158c7a ----
FCSTD DOCUMENT  (FreeCAD 2020.10.16R22739 +2665 (Git))
Label: krokowiec-nema17
License: All rights reserved
LicenseURL: http://en.wikipedia.org/wiki/All_rights_reserved
objects: Sketcher::SketchObject×5, PartDesign::Pad×3, PartDesign::Chamfer×2, PartDesign::Pocket×1, PartDesign::Hole×1, PartDesign::Body×1
note: 27 computed .brp shape members not serialized (recipe doc carries the construction recipe); baked Part::Feature solids carry a one-line shape summary decoded from their .brp

FEATURE [Sketcher::SketchObject] Sketch
  MapMode = 5
  Support = -> [XY_Plane]
  sketch-geometry (5):
    g0: LineSegment StartX=21.15 StartY=21.15 StartZ=0 EndX=-21.15 EndY=21.15 EndZ=0
    g1: LineSegment StartX=-21.15 StartY=21.15 StartZ=0 EndX=-21.15 EndY=-21.15 EndZ=0
    g2: LineSegment StartX=-21.15 StartY=-21.15 StartZ=0 EndX=21.15 EndY=-21.15 EndZ=0
    g3: LineSegment StartX=21.15 StartY=-21.15 StartZ=0 EndX=21.15 EndY=21.15 EndZ=0
    g4: Circle [constr] CenterX=0 CenterY=0 CenterZ=0 NormalX=0 NormalY=0 NormalZ=1 AngleXU=0 Radius=29.9106
  constraints (14):
    c: Coincident(g0,g1)
    c: Coincident(g1,g2)
    c: Coincident(g2,g3)
    c: Coincident(g3,g0)
    c: Equal(g0,g1)
    c: Equal(g0,g2)
    c: Equal(g0,g3)
    c: PointOnObject(g0,g4)
    c: PointOnObject(g1,g4)
    c: PointOnObject(g2,g4)
    c: PointOnObject(g3,g4)
    c: Coincident(g4,g-1)
    c: Horizontal(g0)
    c: DistanceY(g3,g3) = 42.3
FEATURE [PartDesign::Pad] Pad
  ClaimChildren = false
  Direction = (1,1,1)
  Length = 40
  Length2 = 100
  NewSolid = false
  Profile = -> Sketch
  Suppress = false
  Type = 0
FEATURE [Sketcher::SketchObject] Sketch001
  MapMode = 5
  Placement = pos=(0,0,40) rot=(0,0,1;0rad)
  Support = -> [Pad]
  sketch-geometry (1):
    g0: Circle CenterX=0 CenterY=0 CenterZ=0 NormalX=0 NormalY=0 NormalZ=1 AngleXU=0 Radius=11
  constraints (2):
    c: Coincident(g0,g-1)
    c: Diameter(g0) = 22
FEATURE [PartDesign::Pad] Pad001
  BaseFeature = -> Pad
  ClaimChildren = false
  Direction = (1,1,1)
  Length = 2
  Length2 = 100
  NewSolid = false
  Profile = -> Sketch001
  Suppress = false
  Type = 0
FEATURE [Sketcher::SketchObject] Sketch002
  MapMode = 5
  Placement = pos=(0,0,40) rot=(0,0,1;0rad)
  Support = -> [Pad001]
  sketch-geometry (1):
    g0: Circle CenterX=0 CenterY=0 CenterZ=0 NormalX=0 NormalY=0 NormalZ=1 AngleXU=0 Radius=2.5
  constraints (2):
    c: Coincident(g0,g-1)
    c: Diameter(g0) = 5
FEATURE [PartDesign::Pad] Pad002
  BaseFeature = -> Pad001
  ClaimChildren = false
  Direction = (1,1,1)
  Length = 24
  Length2 = 100
  NewSolid = false
  Profile = -> Sketch002
  Suppress = false
  Type = 0
FEATURE [PartDesign::Chamfer] Chamfer
  Angle = 45
  Base = -> Pad002 [Edge18]
  BaseFeature = -> Pad002
  ChamferType = 0
  FlipDirection = false
  NewSolid = false
  Size = 0.5
  Size2 = 1
  SupportTransform = true
  Suppress = false
FEATURE [Sketcher::SketchObject] Sketch003
  ExternalGeometry = -> [Chamfer]
  MapMode = 5
  Placement = pos=(0,0,0) rot=(1,0,0;1.5708rad)
  Support = -> [XZ_Plane]
  sketch-geometry (4):
    g0: LineSegment StartX=2 StartY=64 StartZ=0 EndX=2.5 EndY=64 EndZ=0
    g1: LineSegment StartX=2.5 StartY=64 StartZ=0 EndX=2.5 EndY=43 EndZ=0
    g2: LineSegment StartX=2.5 StartY=43 StartZ=0 EndX=2 EndY=43 EndZ=0
    g3: LineSegment StartX=2 StartY=43 StartZ=0 EndX=2 EndY=64 EndZ=0
  constraints (12):
    c: Coincident(g0,g1)
    c: Coincident(g1,g2)
    c: Coincident(g2,g3)
    c: Coincident(g3,g0)
    c: Horizontal(g0)
    c: Horizontal(g2)
    c: Vertical(g1)
    c: Vertical(g3)
    c: PointOnObject(g0,g-3)
    c: PointOnObject(g1,g-4)
    c: DistanceX(g2,g2) = 0.5
    c: DistanceY(g1,g1) = 21
FEATURE [PartDesign::Pocket] Pocket
  BaseFeature = -> Chamfer
  ClaimChildren = false
  Length = 20
  Length2 = 100
  Midplane = true
  NewSolid = false
  Profile = -> Sketch003
  Suppress = false
  Type = 1
FEATURE [Sketcher::SketchObject] Sketch004
  MapMode = 5
  Placement = pos=(0,0,40) rot=(0,0,1;0rad)
  Support = -> [Pocket]
  sketch-geometry (4):
    g0: Circle CenterX=15.5 CenterY=-15.5 CenterZ=0 NormalX=0 NormalY=0 NormalZ=1 AngleXU=0 Radius=1.25
    g1: Circle CenterX=15.5 CenterY=15.5 CenterZ=0 NormalX=0 NormalY=0 NormalZ=1 AngleXU=0 Radius=1.25
    g2: Circle CenterX=-15.5 CenterY=15.5 CenterZ=0 NormalX=0 NormalY=0 NormalZ=1 AngleXU=0 Radius=1.25
    g3: Circle CenterX=-15.5 CenterY=-15.5 CenterZ=0 NormalX=0 NormalY=0 NormalZ=1 AngleXU=0 Radius=1.25
  constraints (9):
    c: Diameter(g0) = 2.5
    c: Symmetric(g1,g0,g-1)
    c: Symmetric(g1,g2,g-2)
    c: Symmetric(g3,g2,g-1)
    c: Equal(g2,g1)
    c: Equal(g1,g3)
    c: Equal(g3,g0)
    c: DistanceX(g2,g1) = 31
    c: DistanceY(g0,g1) = 31
FEATURE [PartDesign::Hole] Hole
  BaseFeature = -> Pocket
  ClaimChildren = false
  Depth = 4
  DepthType = 0
  Diameter = 1.75
  DrillPoint = 1
  DrillPointAngle = 118
  HoleCutCountersinkAngle = 90
  HoleCutDepth = 0
  HoleCutDiameter = 1.6
  HoleCutType = 0
  ModelActualThread = false
  NewSolid = false
  Profile = -> Sketch004
  Suppress = false
  Tapered = false
  TaperedAngle = 90
  ThreadAngle = 0
  ThreadClass = 0
  ThreadCutOffInner = 0
  ThreadCutOffOuter = 0
  ThreadDirection = 0
  ThreadFit = 0
  ThreadPitch = 0
  ThreadSize = 0
  ThreadType = 1
  Threaded = false
FEATURE [PartDesign::Chamfer] Chamfer001
  Angle = 45
  Base = -> Hole [Edge26,Edge23,Edge28,Edge24]
  BaseFeature = -> Hole
  ChamferType = 0
  FlipDirection = false
  NewSolid = false
  Size = 5
  Size2 = 1
  SupportTransform = true
  Suppress = false
FEATURE [PartDesign::Body] Body  label="nema17"
  ExportMode = 0
  Group = -> [Sketch,Pad,Sketch001,Pad001,Sketch002,Pad002,Chamfer,Sketch003,Pocket,Sketch004,Hole,Chamfer001]
  Origin = -> Origin
  Tip = -> Chamfer001
  _ExportChildren = -> [Pad,Pad001,Pad002,Chamfer,Pocket,Hole,Chamfer001]
  _GroupVersion = 1
---- part oslona-lozyska.FCStd = doc fcstd_f08a9343e0c5 ----
FCSTD DOCUMENT  (FreeCAD 2020.10.16R22739 +2665 (Git))
Label: oslona-lozyska
License: All rights reserved
LicenseURL: http://en.wikipedia.org/wiki/All_rights_reserved
objects: Sketcher::SketchObject×2, PartDesign::Revolution×1, PartDesign::Pocket×1, PartDesign::Chamfer×1, PartDesign::Body×1
note: 12 computed .brp shape members not serialized (recipe doc carries the construction recipe); baked Part::Feature solids carry a one-line shape summary decoded from their .brp

FEATURE [Sketcher::SketchObject] Sketch
  MapMode = 5
  Placement = pos=(0,0,0) rot=(1,0,0;1.5708rad)
  Support = -> [XZ_Plane]
  sketch-geometry (5):
    g0: LineSegment StartX=85 StartY=0 StartZ=0 EndX=85 EndY=28.5 EndZ=0
    g1: LineSegment StartX=85 StartY=28.5 StartZ=0 EndX=84.5 EndY=29 EndZ=0
    g2: LineSegment StartX=84.5 StartY=29 StartZ=0 EndX=87 EndY=29 EndZ=0
    g3: LineSegment StartX=87 StartY=29 StartZ=0 EndX=87 EndY=0 EndZ=0
    g4: LineSegment StartX=87 StartY=0 StartZ=0 EndX=85 EndY=0 EndZ=0
  constraints (15):
    c: PointOnObject(g0,g-1)
    c: Vertical(g0)
    c: Coincident(g0,g1)
    c: Coincident(g1,g2)
    c: Coincident(g2,g3)
    c: PointOnObject(g3,g-1)
    c: Vertical(g3)
    c: Coincident(g3,g4)
    c: Coincident(g4,g0)
    c: Horizontal(g2)
    c: Angle(g1,g2) = 0.785398
    c: DistanceX(g0) = 85
    c: DistanceX(g4,g4) = 2
    c: DistanceX(g2,g2) = 2.5
    c: DistanceY(g3,g3) = 29
FEATURE [PartDesign::Revolution] Revolution
  Angle = 360
  Axis = (0,2e-16,1)
  Base = (0,0,0)
  ClaimChildren = false
  NewSolid = false
  Placement = pos=(0,0,0) rot=(1,0,0;1.5708rad)
  Profile = -> Sketch
  ReferenceAxis = -> Sketch [V_Axis]
  Reversed = true
  Suppress = false
FEATURE [Sketcher::SketchObject] Sketch001
  MapMode = 5
  Placement = pos=(0,0,0) rot=(1,0,0;3.14159rad)
  Support = -> [Revolution]
  sketch-geometry (1):
    g0: Circle CenterX=0 CenterY=0 CenterZ=0 NormalX=0 NormalY=0 NormalZ=1 AngleXU=0 Radius=86
  constraints (2):
    c: Coincident(g0,g-1)
    c: Diameter(g0) = 172
FEATURE [PartDesign::Pocket] Pocket
  BaseFeature = -> Revolution
  ClaimChildren = false
  Length = 25
  Length2 = 100
  NewSolid = false
  Placement = pos=(0,0,0) rot=(1,0,0;1.5708rad)
  Profile = -> Sketch001
  Suppress = false
  Type = 0
FEATURE [PartDesign::Chamfer] Chamfer
  Angle = 45
  Base = -> Pocket [Edge1,Edge8]
  BaseFeature = -> Pocket
  ChamferType = 0
  FlipDirection = false
  NewSolid = false
  Placement = pos=(0,0,0) rot=(1,0,0;1.5708rad)
  Size = 0.5
  Size2 = 1
  SupportTransform = true
  Suppress = false
FEATURE [PartDesign::Body] Body  label="oslona-lozyska"
  ExportMode = 0
  Group = -> [Sketch,Revolution,Sketch001,Pocket,Chamfer]
  Origin = -> Origin
  Tip = -> Chamfer
  _ExportChildren = -> [Revolution,Pocket,Chamfer]
  _GroupVersion = 1
---- part piasta-lozyska2.FCStd = doc fcstd_c5aec694536b ----
FCSTD DOCUMENT  (FreeCAD 2020.10.16R22739 +2665 (Git))
Label: piasta-lozyska2
License: All rights reserved
LicenseURL: http://en.wikipedia.org/wiki/All_rights_reserved
objects: Sketcher::SketchObject×4, PartDesign::Pocket×3, PartDesign::Pad×1, PartDesign::PolarPattern×1, PartDesign::Chamfer×1, PartDesign::Fillet×1, PartDesign::Body×1
note: 25 computed .brp shape members not serialized (recipe doc carries the construction recipe); baked Part::Feature solids carry a one-line shape summary decoded from their .brp

FEATURE [Sketcher::SketchObject] Sketch
  MapMode = 5
  Support = -> [XY_Plane]
  sketch-geometry (1):
    g0: Circle CenterX=0 CenterY=0 CenterZ=0 NormalX=0 NormalY=0 NormalZ=1 AngleXU=0 Radius=66.25
  constraints (2):
    c: Coincident(g0,g-1)
    c: Diameter(g0) = 132.5
FEATURE [PartDesign::Pad] Pad
  ClaimChildren = false
  Direction = (1,1,1)
  Length = 6
  Length2 = 100
  NewSolid = false
  Profile = -> Sketch
  Suppress = false
  Type = 0
FEATURE [Sketcher::SketchObject] Sketch001
  MapMode = 5
  Support = -> [XY_Plane]
  sketch-geometry (1):
    g0: Circle CenterX=0 CenterY=0 CenterZ=0 NormalX=0 NormalY=0 NormalZ=1 AngleXU=0 Radius=5.5
  constraints (2):
    c: Coincident(g0,g-1)
    c: Diameter(g0) = 11
FEATURE [PartDesign::Pocket] Pocket
  BaseFeature = -> Pad
  ClaimChildren = false
  Length = 5
  Length2 = 100
  NewSolid = false
  Profile = -> Sketch001
  Reversed = true
  Suppress = false
  Type = 1
FEATURE [Sketcher::SketchObject] Sketch002
  MapMode = 5
  Support = -> [XY_Plane]
  sketch-geometry (7):
    g0: ArcOfCircle CenterX=0 CenterY=0 CenterZ=0 NormalX=0 NormalY=0 NormalZ=1 AngleXU=0 Radius=60 StartAngle=1.65423 EndAngle=3.58176
    g1: ArcOfCircle CenterX=0 CenterY=0 CenterZ=0 NormalX=0 NormalY=0 NormalZ=1 AngleXU=0 Radius=10 StartAngle=2.0944 EndAngle=3.14159
    g2: LineSegment StartX=-5 StartY=8.66025 StartZ=0 EndX=-5 EndY=59.7913 EndZ=0
    g3: LineSegment [constr] StartX=0 StartY=0 StartZ=0 EndX=-86.6025 EndY=-50 EndZ=0
    g4: LineSegment StartX=-10 StartY=-1e-16 StartZ=0 EndX=-54.2808 EndY=-25.5655 EndZ=0
    g5: LineSegment [constr] StartX=-10 StartY=-1e-16 StartZ=0 EndX=0 EndY=0 EndZ=0
    g6: Circle CenterX=0 CenterY=50 CenterZ=0 NormalX=0 NormalY=0 NormalZ=1 AngleXU=0 Radius=2
  constraints (20):
    c: Coincident(g0,g-1)
    c: Coincident(g1,g0)
    c: Vertical(g2)
    c: Coincident(g3,g0)
    c: Angle(g3) = -2.61799
    c: Parallel(g4,g3)
    c: Diameter(g0) = 120
    c: Coincident(g5,g4)
    c: Coincident(g5,g0)
    c: Coincident(g0,g2)
    c: Coincident(g0,g4)
    c: Coincident(g1,g2)
    c: DistanceX(g1) = -5
    c: Diameter(g1) = 20
    c: Distance(g1,g3) = 5
    c: Coincident(g4,g1)
    c: Distance(g3) = 100
    c: PointOnObject(g6,g-2)
    c: Diameter(g6) = 4
    c: DistanceY(g6) = 50
FEATURE [PartDesign::Pocket] Pocket001
  BaseFeature = -> Pocket
  ClaimChildren = false
  Length = 5
  Length2 = 100
  NewSolid = false
  Profile = -> Sketch002
  Reversed = true
  Suppress = false
  Type = 1
FEATURE [PartDesign::PolarPattern] PolarPattern
  Angle = 360
  Axis = -> Sketch002 [N_Axis]
  BaseFeature = -> Pocket001
  CopyShape = false
  NewSolid = false
  Occurrences = 3
  OriginalSubs = -> [Pocket001]
  Originals = -> [Pocket001]
  SubTransform = true
  Suppress = false
FEATURE [PartDesign::Chamfer] Chamfer
  Angle = 45
  Base = -> PolarPattern [Edge3,Edge2]
  BaseFeature = -> PolarPattern
  ChamferType = 0
  FlipDirection = false
  NewSolid = false
  Size = 1
  Size2 = 1
  SupportTransform = true
  Suppress = false
FEATURE [PartDesign::Fillet] Fillet
  Base = -> Chamfer [Edge49,Edge46,Edge54,Edge52,Edge42,Edge40]
  BaseFeature = -> Chamfer
  NewSolid = false
  Radius = 6
  SupportTransform = true
  Suppress = false
FEATURE [Sketcher::SketchObject] Sketch003
  MapMode = 5
  Placement = pos=(0,0,6) rot=(0,0,1;0rad)
  Support = -> [Fillet]
  sketch-geometry (1):
    g0: Circle CenterX=0 CenterY=0 CenterZ=0 NormalX=0 NormalY=0 NormalZ=1 AngleXU=0 Radius=64
  constraints (2):
    c: Coincident(g0,g-1)
    c: Diameter(g0) = 128
FEATURE [PartDesign::Pocket] Pocket002
  BaseFeature = -> Fillet
  ClaimChildren = false
  Length = 3
  Length2 = 100
  NewSolid = false
  Profile = -> Sketch003
  Suppress = false
  Type = 0
FEATURE [PartDesign::Body] Body  label="piasta-lozyska2"
  ExportMode = 0
  Group = -> [Sketch,Pad,Sketch001,Pocket,Sketch002,Pocket001,PolarPattern,Chamfer,Fillet,Sketch003,Pocket002]
  Origin = -> Origin
  Tip = -> Pocket002
  _ExportChildren = -> [Pad,Pocket,Pocket001,PolarPattern,Chamfer,Fillet,Pocket002]
  _GroupVersion = 1
---- part plyta-boczna.fcstd = doc fcstd_4c2c7915aa8b ----
FCSTD DOCUMENT  (FreeCAD 2020.10.16R22739 +2665 (Git))
Label: plyta-boczna
License: All rights reserved
LicenseURL: http://en.wikipedia.org/wiki/All_rights_reserved
objects: Sketcher::SketchObject×3, PartDesign::Pad×1, PartDesign::Pocket×1, PartDesign::Line×1, PartDesign::Body×1
note: 11 computed .brp shape members not serialized (recipe doc carries the construction recipe); baked Part::Feature solids carry a one-line shape summary decoded from their .brp

FEATURE [Sketcher::SketchObject] Sketch
  MapMode = 5
  Placement = pos=(0,0,0) rot=(0.57735,0.57735,0.57735;2.0944rad)
  Support = -> [YZ_Plane]
  sketch-geometry (5):
    g0: ArcOfCircle CenterX=0 CenterY=580 CenterZ=0 NormalX=0 NormalY=0 NormalZ=1 AngleXU=0 Radius=95 StartAngle=0.495618 EndAngle=3.41262
    g1: ArcOfCircle CenterX=-765.98 CenterY=367.162 CenterZ=0 NormalX=0 NormalY=0 NormalZ=1 AngleXU=0 Radius=700 StartAngle=5.73104 EndAngle=6.55421
    g2: ArcOfCircle CenterX=-708.138 CenterY=197.162 CenterZ=0 NormalX=0 NormalY=0 NormalZ=1 AngleXU=0 Radius=900 StartAngle=6.06233 EndAngle=6.7788
    g3: LineSegment StartX=-170 StartY=0 StartZ=0 EndX=170 EndY=0 EndZ=0
    g4: Circle CenterX=0 CenterY=580 CenterZ=0 NormalX=0 NormalY=0 NormalZ=1 AngleXU=0 Radius=6
  constraints (16):
    c: PointOnObject(g0,g-2)
    c: Radius(g0) = 95
    c: DistanceY(g-1,g0) = 580
    c: PointOnObject(g1,g-1)
    c: PointOnObject(g2,g-1)
    c: Tangent(g2,g0)
    c: Coincident(g3,g1)
    c: Coincident(g3,g2)
    c: DistanceX(g3,g3) = 340
    c: DistanceX(g1,g-1) = 170
    c: Radius(g1) = 700
    c: Radius(g2) = 900
    c: Coincident(g0,g2)
    c: Tangent(g0,g1) = 1.5708
    c: Coincident(g4,g0)
    c: Radius(g4) = 6
FEATURE [PartDesign::Pad] Pad
  AllowMultiFace = false
  ClaimChildren = false
  Direction = (1,1,1)
  Length = 18
  Length2 = 100
  Midplane = true
  NewSolid = false
  Placement = pos=(0,0,0) rot=(0.57735,0.57735,0.57735;2.0944rad)
  Profile = -> Sketch
  Suppress = false
  Type = 0
FEATURE [Sketcher::SketchObject] Sketch001
  ExternalGeometry = -> [Pad]
  MapMode = 5
  Placement = pos=(9,-1.0152e-12,1.0162e-12) rot=(0.57735,0.57735,0.57735;2.0944rad)
  Support = -> [Pad]
  sketch-geometry (5):
    g0: Circle [constr] CenterX=0 CenterY=580 CenterZ=0 NormalX=0 NormalY=0 NormalZ=1 AngleXU=0 Radius=75
    g1: LineSegment [constr] StartX=0 StartY=580 StartZ=0 EndX=-53.033 EndY=526.967 EndZ=0
    g2: LineSegment [constr] StartX=0 StartY=580 StartZ=0 EndX=53.033 EndY=526.967 EndZ=0
    g3: Circle CenterX=-53.033 CenterY=526.967 CenterZ=0 NormalX=0 NormalY=0 NormalZ=1 AngleXU=0 Radius=3
    g4: Circle CenterX=53.033 CenterY=526.967 CenterZ=0 NormalX=0 NormalY=0 NormalZ=1 AngleXU=0 Radius=3
  constraints (12):
    c: Coincident(g0,g-3)
    c: Coincident(g1,g0)
    c: PointOnObject(g1,g0)
    c: Coincident(g2,g0)
    c: PointOnObject(g2,g0)
    c: Angle(g1,g2) = 1.5708
    c: Angle(g1) = -2.35619
    c: Radius(g0) = 75
    c: Coincident(g3,g1)
    c: Coincident(g4,g2)
    c: Equal(g4,g3)
    c: Radius(g4) = 3
FEATURE [PartDesign::Pocket] Pocket
  AllowMultiFace = false
  BaseFeature = -> Pad
  ClaimChildren = false
  Length = 5
  Length2 = 100
  NewSolid = false
  Placement = pos=(0,0,0) rot=(0.57735,0.57735,0.57735;2.0944rad)
  Profile = -> Sketch001
  Suppress = false
  Type = 1
FEATURE [PartDesign::Line] DatumLine
  AttacherType = Attacher::AttachEngineLine
  Length = 18
  MapMode = 19
  Placement = pos=(9,6.45235e-11,580) rot=(0.57735,0.57735,0.57735;2.0944rad)
  ResizeMode = 0
  Support = -> [Pocket]
FEATURE [Sketcher::SketchObject] Sketch002
  ExternalGeometry = -> [Pocket]
  MapMode = 5
  Placement = pos=(9,-1.0152e-12,1.0162e-12) rot=(0.57735,0.57735,0.57735;2.0944rad)
  Support = -> [Pocket]
  sketch-geometry (1):
    g0: LineSegment StartX=2.416e-13 StartY=580 StartZ=0 EndX=0 EndY=0 EndZ=0
  constraints (2):
    c: Coincident(g0,g-3)
    c: Coincident(g0,g-1)
FEATURE [PartDesign::Body] Body  label="plyta-boczna"
  ExportMode = 0
  Group = -> [Sketch,Pad,Sketch001,Pocket,DatumLine,Sketch002]
  Origin = -> Origin
  SingleSolid = true
  Tip = -> Pocket
  _ExportChildren = -> [Pad,Pocket,DatumLine,Sketch002]
  _GroupVersion = 1
---- part plyta-okr-gora.fcstd = doc fcstd_dba669465c97 ----
FCSTD DOCUMENT  (FreeCAD 2020.12.13R23076 +3015 (Git))
Label: plyta-okr-gora
License: All rights reserved
LicenseURL: http://en.wikipedia.org/wiki/All_rights_reserved
objects: Sketcher::SketchObject×3, PartDesign::Pad×1, PartDesign::Pocket×1, PartDesign::Body×1
note: 10 computed .brp shape members not serialized (recipe doc carries the construction recipe); baked Part::Feature solids carry a one-line shape summary decoded from their .brp

FEATURE [Sketcher::SketchObject] Sketch
  MapMode = 5
  Support = -> [XY_Plane]
  sketch-geometry (1):
    g0: Circle CenterX=0 CenterY=0 CenterZ=0 NormalX=0 NormalY=0 NormalZ=1 AngleXU=0 Radius=260
  constraints (2):
    c: Coincident(g0,g-1)
    c: Radius(g0) = 260
FEATURE [PartDesign::Pad] Pad
  AllowMultiFace = false
  ClaimChildren = false
  Direction = (1,1,1)
  Fit = 0
  FitJoin = 0
  InnerFit = 0
  InnerFitJoin = 0
  InnerTaperAngle = 0
  InnerTaperAngleRev = 0
  Length = 18
  Length2 = 100
  NewSolid = false
  Profile = -> Sketch
  Suppress = false
  Type = 0
FEATURE [Sketcher::SketchObject] Sketch001
  MapMode = 5
  Support = -> [XY_Plane]
  sketch-geometry (1):
    g0: Circle CenterX=0 CenterY=0 CenterZ=0 NormalX=0 NormalY=0 NormalZ=1 AngleXU=0 Radius=7
  constraints (2):
    c: Coincident(g0,g-1)
    c: Diameter(g0) = 14
FEATURE [PartDesign::Pocket] Pocket
  BaseFeature = -> Pad
  ClaimChildren = false
  Fit = 0
  FitJoin = 0
  InnerFit = 0
  InnerFitJoin = 0
  InnerTaperAngle = 0
  InnerTaperAngleRev = 0
  Length = 5
  Length2 = 100
  NewSolid = false
  Profile = -> Sketch001
  Reversed = true
  Suppress = false
  Type = 1
FEATURE [Sketcher::SketchObject] Sketch002
  MapMode = 5
  Placement = pos=(0,0,18) rot=(0,0,1;0rad)
  Support = -> [Pocket]
  sketch-geometry (4):
    g0: LineSegment StartX=-170 StartY=150 StartZ=0 EndX=170 EndY=150 EndZ=0
    g1: LineSegment StartX=-170 StartY=150 StartZ=0 EndX=-170 EndY=0 EndZ=0
    g2: LineSegment StartX=170 StartY=150 StartZ=0 EndX=170 EndY=0 EndZ=0
    g3: LineSegment StartX=-28 StartY=-227 StartZ=0 EndX=28 EndY=-227 EndZ=0
  constraints (12):
    c: Symmetric(g0,g0,g-2)
    c: DistanceX(g0,g0) = 340
    c: DistanceY(g0) = 150
    c: Coincident(g1,g0)
    c: PointOnObject(g1,g-1)
    c: Vertical(g1)
    c: Coincident(g2,g0)
    c: PointOnObject(g2,g-1)
    c: Vertical(g2)
    c: Symmetric(g3,g3,g-2)
    c: DistanceX(g3,g3) = 56
    c: DistanceY(g3) = -227
FEATURE [PartDesign::Body] Body  label="plyta-okr-gora"
  ExportMode = 0
  Group = -> [Sketch,Pad,Sketch001,Pocket,Sketch002]
  Origin = -> Origin
  SingleSolid = true
  Tip = -> Pocket
  _ExportChildren = -> [Pad,Pocket,Sketch002]
  _GroupVersion = 1
---- part plyta-tylna.fcstd = doc fcstd_d55265bc2517 ----
FCSTD DOCUMENT  (FreeCAD 0.19R21911 +2545 (Git))
Label: plyta-tylna
License: All rights reserved
LicenseURL: http://en.wikipedia.org/wiki/All_rights_reserved
objects: Sketcher::SketchObject×1, PartDesign::Pad×1, PartDesign::Body×1
note: 5 computed .brp shape members not serialized (recipe doc carries the construction recipe); baked Part::Feature solids carry a one-line shape summary decoded from their .brp

FEATURE [Sketcher::SketchObject] Sketch
  MapMode = 5
  Placement = pos=(0,0,0) rot=(1,0,0;1.5708rad)
  Support = -> [XZ_Plane]
  sketch-geometry (7):
    g0: LineSegment StartX=-170 StartY=0 StartZ=0 EndX=170 EndY=0 EndZ=0
    g1: LineSegment StartX=170 StartY=0 StartZ=0 EndX=170 EndY=380 EndZ=0
    g2: LineSegment StartX=170 StartY=380 StartZ=0 EndX=90 EndY=380 EndZ=0
    g3: LineSegment StartX=-170 StartY=380 StartZ=0 EndX=-170 EndY=0 EndZ=0
    g4: ArcOfCircle CenterX=0 CenterY=500 CenterZ=0 NormalX=0 NormalY=0 NormalZ=1 AngleXU=0 Radius=150 StartAngle=4.06889 EndAngle=5.35589
    g5: LineSegment StartX=-90 StartY=380 StartZ=0 EndX=-170 EndY=380 EndZ=0
    g6: GeomPoint X=0 Y=350 Z=0
  constraints (19):
    c: Coincident(g0,g1)
    c: Coincident(g1,g2)
    c: Coincident(g5,g3)
    c: Coincident(g3,g0)
    c: Horizontal(g0)
    c: Vertical(g1)
    c: Vertical(g3)
    c: PointOnObject(g0,g-1)
    c: Symmetric(g1,g5,g-2)
    c: DistanceY(g1,g1) = 380
    c: DistanceX(g0,g0) = 340
    c: Tangent(g2,g5)
    c: Coincident(g4,g5)
    c: Coincident(g4,g2)
    c: PointOnObject(g4,g-2)
    c: PointOnObject(g6,g-2)
    c: PointOnObject(g6,g4)
    c: DistanceY(g-1,g6) = 350
    c: DistanceX(g4,g2) = 180
FEATURE [PartDesign::Pad] Pad
  AllowMultiFace = false
  ClaimChildren = false
  Length = 18
  Length2 = 100
  Placement = pos=(0,0,0) rot=(1,0,0;1.5708rad)
  Profile = -> Sketch
  Suppress = false
  Type = 0
FEATURE [PartDesign::Body] Body  label="plyta-tylna"
  ExportMode = 0
  Group = -> [Sketch,Pad]
  Origin = -> Origin
  SingleSolid = true
  Tip = -> Pad
  _ExportChildren = -> [Pad]
  _GroupVersion = 1
---- part przekladnia.FCStd = doc fcstd_56c9d12a02b7 ----
FCSTD DOCUMENT  (FreeCAD 2020.12.13R23076 +3015 (Git))
Label: przekladnia
License: All rights reserved
LicenseURL: http://en.wikipedia.org/wiki/All_rights_reserved
objects: Part::FeaturePython×44, App::FeaturePython×43, App::Link×7
note: 43 computed .brp shape members not serialized (recipe doc carries the construction recipe); baked Part::Feature solids carry a one-line shape summary decoded from their .brp
EXTERNAL_REF file=plytaprzekladni.FCStd obj=Body
EXTERNAL_REF file=krokowiec-nema17.FCStd obj=Body
EXTERNAL_REF file=kolkozebmodul1fi5przekl.FCStd obj=Body
EXTERNAL_REF file=lozysko 5201.FCStd obj=Body
EXTERNAL_REF file=koloprzekladni.FCStd obj=Body
EXTERNAL_REF file=m8x40imb.FCStd obj=Body
EXTERNAL_REF file=wkladkaloz.FCStd obj=Body

FEATURE [App::Link] Link001  label="plyta-przekadni"
  LinkPlacement = pos=(0,0,0) rot=(-1,0,0;3.14159rad)
  LinkedObject = -> <external plytaprzekladni.FCStd>#Body
  Placement = pos=(0,0,0) rot=(-1,0,0;3.14159rad)
  SyncGroupVisibility = false
  _LinkVersion = 1
FEATURE [App::Link] Link003  label="nema17"
  LinkPlacement = pos=(0.85,0.15,24) rot=(1,0,0;3.14159rad)
  LinkedObject = -> <external krokowiec-nema17.FCStd>#Body
  Placement = pos=(0.85,0.15,24) rot=(1,0,0;3.14159rad)
  SyncGroupVisibility = false
  _LinkVersion = 1
FEATURE [App::Link] Link  label="kolkozebstozniskie"
  LinkPlacement = pos=(0.85,0.15,-31) rot=(0,0,-1;0.012799rad)
  LinkedObject = -> <external kolkozebmodul1fi5przekl.FCStd>#Body
  Placement = pos=(0.85,0.15,-31) rot=(0,0,-1;0.012799rad)
  SyncGroupVisibility = false
  _LinkVersion = 1
FEATURE [App::Link] Link004  label="lozysko5201"
  LinkPlacement = pos=(-40,1.5e-15,-11.95) rot=(0,0,-1;0.034901rad)
  LinkedObject = -> <external lozysko 5201.FCStd>#Body
  Placement = pos=(-40,1.5e-15,-11.95) rot=(0,0,-1;0.034901rad)
  SyncGroupVisibility = false
  _LinkVersion = 1
FEATURE [App::Link] Link006  label="koloprzekladni"
  LinkPlacement = pos=(-40,3.8e-15,-30.9) rot=(-0.999741,0.022763,0;3.14159rad)
  LinkedObject = -> <external koloprzekladni.FCStd>#Body
  Placement = pos=(-40,3.8e-15,-30.9) rot=(-0.999741,0.022763,0;3.14159rad)
  SyncGroupVisibility = false
  _LinkVersion = 1
FEATURE [App::Link] Link007  label="m8x40imb"
  LinkPlacement = pos=(-40,5.4e-15,-43.9) rot=(0,0,-1;0.002436rad)
  LinkedObject = -> <external m8x40imb.FCStd>#Body
  Placement = pos=(-40,5.4e-15,-43.9) rot=(0,0,-1;0.002436rad)
  SyncGroupVisibility = false
  _LinkVersion = 1
FEATURE [App::Link] Link005  label="wkladkamimosr"
  LinkPlacement = pos=(-40,2.5e-15,-20.9) rot=(0,0,1;3.95082rad)
  LinkedObject = -> <external wkladkaloz.FCStd>#Body
  Placement = pos=(-40,2.5e-15,-20.9) rot=(0,0,1;3.95082rad)
  SyncGroupVisibility = false
  _LinkVersion = 1
FEATURE [Part::FeaturePython] Parts  # WARN: FeaturePython — macro-defined, semantics opaque (R4)
  Group = -> [Link001,Link003,Link,Link004,Link006,Link007,Link005]
  GroupMode = 0
  _LinkVersion = 1
FEATURE [Part::FeaturePython] Assembly  label="przekladnia"  # WARN: FeaturePython — macro-defined, semantics opaque (R4)
  AutoRelax = true
  BuildShape = 0
  Freeze = false
  Group = -> [Constraints,Elements,Parts]
  Verbose = false
  _LinkVersion = 1
  _SolverType = 1
  _Version = 1
FEATURE [App::FeaturePython] Constraints  # WARN: FeaturePython — macro-defined, semantics opaque (R4)
  Group = -> [Constraint,Constraint002,Constraint005,Constraint015,Constraint016,Constraint020,Constraint021,Constraint022,Constraint023,Constraint024,Constraint025,Constraint026,Constraint027,Constraint028]
  _LinkVersion = 1
  _Version = 1
FEATURE [App::FeaturePython] Elements  # WARN: FeaturePython — macro-defined, semantics opaque (R4)
  Group = -> [_Element,_Element001,_Element002,_Element003,_Element004,_Element006,_Element007,_Element009,_Element010,_Element011,_Element012,_Element014,_Element016,_Element017,_Element019,_Element022,_Element023,_Element024,_Element025,_Element028,Element,Element001,_Element029,_Element030,_Element031,_Element032,_Element033,_Element034,_Element035,_Element036,_Element037,_Element038,_Element039,_Element040,+8 more]
  _LinkVersion = 1
FEATURE [App::FeaturePython] Constraint  label="Locked"  # WARN: FeaturePython — macro-defined, semantics opaque (R4)
  Disabled = false
  Group = -> [ElementLink]
  _ConstraintType = 0
  _LinkVersion = 1
  _Parent = -> Constraints
FEATURE [App::FeaturePython] ElementLink  label="_Element"  # link proxy (typed FeaturePython)
  LinkTransform = true
  LinkedObject = -> _Element
  _LinkVersion = 1
  _Parent = -> Constraint
FEATURE [Part::FeaturePython] _Element  # link proxy (typed FeaturePython)
  Detach = false
  LinkTransform = true
  LinkedObject = -> Link001 [Pocket005.Face1]
  _LinkVersion = 1
  _Parent = -> Elements
FEATURE [Part::FeaturePython] _Element001  # link proxy (typed FeaturePython)
  Detach = false
  LinkTransform = true
  LinkedObject = -> Link001 [Pocket005.Face57]
  _LinkVersion = 1
  _Parent = -> Elements
FEATURE [Part::FeaturePython] _Element002  # link proxy (typed FeaturePython)
  Detach = false
  LinkTransform = true
  LinkedObject = -> Link003 [Chamfer001.Face13]
  _LinkVersion = 1
  _Parent = -> Elements
FEATURE [Part::FeaturePython] _Element003  # link proxy (typed FeaturePython)
  Detach = false
  LinkTransform = true
  LinkedObject = -> Link003 [Chamfer001.Face1]
  _LinkVersion = 1
  _Parent = -> Elements
FEATURE [Part::FeaturePython] _Element004  # link proxy (typed FeaturePython)
  Detach = false
  LinkTransform = true
  LinkedObject = -> Link001 [Pocket005.Face52]
  _LinkVersion = 1
  _Parent = -> Elements
FEATURE [Part::FeaturePython] _Element006  # link proxy (typed FeaturePython)
  Detach = false
  LinkTransform = true
  LinkedObject = -> Link003 [Chamfer001.Face21]
  _LinkVersion = 1
  _Parent = -> Elements
FEATURE [Part::FeaturePython] _Element007  # link proxy (typed FeaturePython)
  Detach = false
  LinkTransform = true
  LinkedObject = -> Link003 [Chamfer001.Face22]
  _LinkVersion = 1
  _Parent = -> Elements
FEATURE [App::FeaturePython] Constraint005  label="AxialAlignment002"  # WARN: FeaturePython — macro-defined, semantics opaque (R4)
  Angle = 0
  AnglePitch = 0
  AngleRoll = 0
  Disabled = false
  Group = -> [ElementLink009,ElementLink010]
  LockAngle = false
  Multiply = false
  _ConstraintType = 36
  _LinkVersion = 1
  _Parent = -> Constraints
FEATURE [App::FeaturePython] ElementLink009  label="_Element009"  # link proxy (typed FeaturePython)
  LinkTransform = true
  LinkedObject = -> _Element009
  _LinkVersion = 1
  _Parent = -> Constraint005
FEATURE [Part::FeaturePython] _Element009  # link proxy (typed FeaturePython)
  Detach = false
  LinkTransform = true
  LinkedObject = -> Link001 [Pocket005.Face54]
  _LinkVersion = 1
  _Parent = -> Elements
FEATURE [App::FeaturePython] ElementLink010  label="_Element010"  # link proxy (typed FeaturePython)
  LinkTransform = true
  LinkedObject = -> _Element010
  _LinkVersion = 1
  _Parent = -> Constraint005
FEATURE [Part::FeaturePython] _Element010  # link proxy (typed FeaturePython)
  Detach = false
  LinkTransform = true
  LinkedObject = -> Link004 [Mirrored.Face1]
  _LinkVersion = 1
  _Parent = -> Elements
FEATURE [Part::FeaturePython] _Element011  # link proxy (typed FeaturePython)
  Detach = false
  LinkTransform = true
  LinkedObject = -> Link004 [Mirrored.Face3]
  _LinkVersion = 1
  _Parent = -> Elements
FEATURE [Part::FeaturePython] _Element012  # link proxy (typed FeaturePython)
  Detach = false
  LinkTransform = true
  LinkedObject = -> Link001 [Pocket005.Face51]
  _LinkVersion = 1
  _Parent = -> Elements
FEATURE [Part::FeaturePython] _Element014  # link proxy (typed FeaturePython)
  Detach = false
  LinkTransform = true
  LinkedObject = -> Link004 [Mirrored.Face12]
  _LinkVersion = 1
  _Parent = -> Elements
FEATURE [Part::FeaturePython] _Element016  # link proxy (typed FeaturePython)
  Detach = false
  LinkTransform = true
  LinkedObject = -> Link004 [Mirrored.Face10]
  _LinkVersion = 1
  _Parent = -> Elements
FEATURE [Part::FeaturePython] _Element017  # link proxy (typed FeaturePython)
  Detach = false
  LinkTransform = true
  LinkedObject = -> Link006 [Groove.Face259]
  _LinkVersion = 1
  _Parent = -> Elements
FEATURE [Part::FeaturePython] _Element019  # link proxy (typed FeaturePython)
  Detach = false
  LinkTransform = true
  LinkedObject = -> Link006 [Groove.Edge264]
  _LinkVersion = 1
  _Parent = -> Elements
FEATURE [Part::FeaturePython] _Element022  # link proxy (typed FeaturePython)
  Detach = false
  LinkTransform = true
  LinkedObject = -> Link006 [Groove.Face4]
  _LinkVersion = 1
  _Parent = -> Elements
FEATURE [Part::FeaturePython] _Element023  # link proxy (typed FeaturePython)
  Detach = false
  LinkTransform = true
  LinkedObject = -> Link007 [BaseFeature.Face4]
  _LinkVersion = 1
  _Parent = -> Elements
FEATURE [Part::FeaturePython] _Element024  # link proxy (typed FeaturePython)
  Detach = false
  LinkTransform = true
  LinkedObject = -> Link007 [BaseFeature.Face2]
  _LinkVersion = 1
  _Parent = -> Elements
FEATURE [Part::FeaturePython] _Element025  # link proxy (typed FeaturePython)
  Detach = false
  LinkTransform = true
  LinkedObject = -> Link006 [Groove.Face380]
  _LinkVersion = 1
  _Parent = -> Elements
FEATURE [Part::FeaturePython] _Element028  # link proxy (typed FeaturePython)
  Detach = false
  LinkTransform = true
  LinkedObject = -> Link003 [Chamfer001.Face23]
  _LinkVersion = 1
  _Parent = -> Elements
FEATURE [Part::FeaturePython] Element  # link proxy (typed FeaturePython)
  Detach = false
  LinkTransform = true
  LinkedObject = -> Link001 [MultiTransform001.Face47]
  _LinkVersion = 1
  _Parent = -> Elements
FEATURE [Part::FeaturePython] Element001  # link proxy (typed FeaturePython)
  Detach = false
  LinkTransform = true
  LinkedObject = -> Link001 [MultiTransform001.Face1]
  _LinkVersion = 1
  _Parent = -> Elements
FEATURE [App::FeaturePython] ElementLink003  label="_Element003"  # link proxy (typed FeaturePython)
  LinkTransform = true
  LinkedObject = -> _Element003
  _LinkVersion = 1
  _Parent = -> Constraint002
FEATURE [App::FeaturePython] ElementLink004  label="_Element004"  # link proxy (typed FeaturePython)
  LinkTransform = true
  LinkedObject = -> _Element004
  _LinkVersion = 1
  _Parent = -> Constraint002
FEATURE [App::FeaturePython] Constraint002  label="PlaneAlignment"  # WARN: FeaturePython — macro-defined, semantics opaque (R4)
  Angle = 0
  AnglePitch = 0
  AngleRoll = 0
  Cascade = false
  Disabled = false
  Group = -> [ElementLink003,ElementLink004]
  LockAngle = false
  _ConstraintType = 37
  _LinkVersion = 1
  _Parent = -> Constraints
FEATURE [App::FeaturePython] Constraint015  label="MultiParallel"  # WARN: FeaturePython — macro-defined, semantics opaque (R4)
  Angle = 0
  AnglePitch = 0
  AngleRoll = 0
  Disabled = false
  Group = -> [ElementLink029,ElementLink030]
  LockAngle = false
  _ConstraintType = 291
  _LinkVersion = 1
  _Parent = -> Constraints
FEATURE [App::FeaturePython] ElementLink029  label="_Element029"  # link proxy (typed FeaturePython)
  LinkTransform = true
  LinkedObject = -> _Element029
  _LinkVersion = 1
  _Parent = -> Constraint015
FEATURE [Part::FeaturePython] _Element029  # link proxy (typed FeaturePython)
  Detach = false
  LinkTransform = true
  LinkedObject = -> Link003 [Chamfer001.Face5]
  _LinkVersion = 1
  _Parent = -> Elements
FEATURE [App::FeaturePython] ElementLink030  label="_Element030"  # link proxy (typed FeaturePython)
  LinkTransform = true
  LinkedObject = -> _Element030
  _LinkVersion = 1
  _Parent = -> Constraint015
FEATURE [Part::FeaturePython] _Element030  # link proxy (typed FeaturePython)
  Detach = false
  LinkTransform = true
  LinkedObject = -> Link001 [MultiTransform001.Face44]
  _LinkVersion = 1
  _Parent = -> Elements
FEATURE [App::FeaturePython] Constraint016  label="PointsPlaneDistance"  # WARN: FeaturePython — macro-defined, semantics opaque (R4)
  Disabled = false
  Distance = -1
  Group = -> [ElementLink031,ElementLink032]
  _ConstraintType = 7
  _LinkVersion = 1
  _Parent = -> Constraints
FEATURE [App::FeaturePython] ElementLink031  label="_Element031"  # link proxy (typed FeaturePython)
  LinkTransform = true
  LinkedObject = -> _Element031
  _LinkVersion = 1
  _Parent = -> Constraint016
FEATURE [Part::FeaturePython] _Element031  # link proxy (typed FeaturePython)
  Detach = false
  LinkTransform = true
  LinkedObject = -> Link003 [Chamfer001.Vertex3]
  _LinkVersion = 1
  _Parent = -> Elements
FEATURE [App::FeaturePython] ElementLink032  label="_Element030"  # link proxy (typed FeaturePython)
  LinkTransform = true
  LinkedObject = -> _Element030
  _LinkVersion = 1
  _Parent = -> Constraint016
FEATURE [Part::FeaturePython] _Element032  # link proxy (typed FeaturePython)
  Detach = false
  LinkTransform = true
  LinkedObject = -> Link [Chamfer.Vertex2]
  _LinkVersion = 1
  _Parent = -> Elements
FEATURE [App::FeaturePython] Constraint020  label="AxialAlignment"  # WARN: FeaturePython — macro-defined, semantics opaque (R4)
  Angle = 0
  AnglePitch = 0
  AngleRoll = 0
  Disabled = false
  Group = -> [ElementLink039,ElementLink040]
  LockAngle = false
  Multiply = false
  _ConstraintType = 36
  _LinkVersion = 0
  _Parent = -> Constraints
FEATURE [App::FeaturePython] ElementLink039  label="_Element010"  # link proxy (typed FeaturePython)
  LinkTransform = true
  LinkedObject = -> _Element010
  _LinkVersion = 0
  _Parent = -> Constraint020
FEATURE [App::FeaturePython] ElementLink040  label="_Element033"  # link proxy (typed FeaturePython)
  LinkTransform = true
  LinkedObject = -> _Element033
  _LinkVersion = 0
  _Parent = -> Constraint020
FEATURE [Part::FeaturePython] _Element033  # link proxy (typed FeaturePython)
  Detach = false
  LinkTransform = true
  LinkedObject = -> Link001 [MultiTransform001.Face51]
  _LinkVersion = 0
  _Parent = -> Elements
FEATURE [Part::FeaturePython] _Element034  # link proxy (typed FeaturePython)
  Detach = false
  LinkTransform = true
  LinkedObject = -> Link004 [Mirrored.Vertex2]
  _LinkVersion = 0
  _Parent = -> Elements
FEATURE [Part::FeaturePython] _Element035  # link proxy (typed FeaturePython)
  Detach = false
  LinkTransform = true
  LinkedObject = -> Link001 [MultiTransform001.Face49]
  _LinkVersion = 0
  _Parent = -> Elements
FEATURE [App::FeaturePython] Constraint021  label="PointInPlane001"  # WARN: FeaturePython — macro-defined, semantics opaque (R4)
  Disabled = false
  Group = -> [ElementLink041,ElementLink042]
  _ConstraintType = 3
  _LinkVersion = 0
  _Parent = -> Constraints
FEATURE [App::FeaturePython] ElementLink041  label="_Element034"  # link proxy (typed FeaturePython)
  LinkTransform = true
  LinkedObject = -> _Element034
  _LinkVersion = 0
  _Parent = -> Constraint021
FEATURE [App::FeaturePython] ElementLink042  label="_Element035"  # link proxy (typed FeaturePython)
  LinkTransform = true
  LinkedObject = -> _Element035
  _LinkVersion = 0
  _Parent = -> Constraint021
FEATURE [App::FeaturePython] Constraint022  label="AxialAlignment003"  # WARN: FeaturePython — macro-defined, semantics opaque (R4)
  Angle = 0
  AnglePitch = 0
  AngleRoll = 0
  Disabled = false
  Group = -> [ElementLink043,ElementLink044]
  LockAngle = false
  Multiply = false
  _ConstraintType = 36
  _LinkVersion = 0
  _Parent = -> Constraints
FEATURE [App::FeaturePython] ElementLink043  label="_Element036"  # link proxy (typed FeaturePython)
  LinkTransform = true
  LinkedObject = -> _Element036
  _LinkVersion = 0
  _Parent = -> Constraint022
FEATURE [Part::FeaturePython] _Element036  # link proxy (typed FeaturePython)
  Detach = false
  LinkTransform = true
  LinkedObject = -> Link005 [Pocket.Face1]
  _LinkVersion = 0
  _Parent = -> Elements
FEATURE [App::FeaturePython] ElementLink044  label="_Element014"  # link proxy (typed FeaturePython)
  LinkTransform = true
  LinkedObject = -> _Element014
  _LinkVersion = 0
  _Parent = -> Constraint022
FEATURE [App::FeaturePython] Constraint023  label="PointInPlane002"  # WARN: FeaturePython — macro-defined, semantics opaque (R4)
  Disabled = false
  Group = -> [ElementLink045,ElementLink046]
  _ConstraintType = 3
  _LinkVersion = 0
  _Parent = -> Constraints
FEATURE [App::FeaturePython] ElementLink045  label="_Element037"  # link proxy (typed FeaturePython)
  LinkTransform = true
  LinkedObject = -> _Element037
  _LinkVersion = 0
  _Parent = -> Constraint023
FEATURE [Part::FeaturePython] _Element037  # link proxy (typed FeaturePython)
  Detach = false
  LinkTransform = true
  LinkedObject = -> Link005 [Pocket.Vertex4]
  _LinkVersion = 0
  _Parent = -> Elements
FEATURE [App::FeaturePython] ElementLink046  label="_Element016"  # link proxy (typed FeaturePython)
  LinkTransform = true
  LinkedObject = -> _Element016
  _LinkVersion = 0
  _Parent = -> Constraint023
FEATURE [App::FeaturePython] Constraint024  label="AxialAlignment004"  # WARN: FeaturePython — macro-defined, semantics opaque (R4)
  Angle = 0
  AnglePitch = 0
  AngleRoll = 0
  Disabled = false
  Group = -> [ElementLink047,ElementLink048]
  LockAngle = false
  Multiply = false
  _ConstraintType = 36
  _LinkVersion = 0
  _Parent = -> Constraints
FEATURE [App::FeaturePython] ElementLink047  label="_Element038"  # link proxy (typed FeaturePython)
  LinkTransform = true
  LinkedObject = -> _Element038
  _LinkVersion = 0
  _Parent = -> Constraint024
FEATURE [Part::FeaturePython] _Element038  # link proxy (typed FeaturePython)
  Detach = false
  LinkTransform = true
  LinkedObject = -> Link005 [Pocket.Face5]
  _LinkVersion = 0
  _Parent = -> Elements
FEATURE [App::FeaturePython] ElementLink048  label="_Element039"  # link proxy (typed FeaturePython)
  LinkTransform = true
  LinkedObject = -> _Element039
  _LinkVersion = 0
  _Parent = -> Constraint024
FEATURE [Part::FeaturePython] _Element039  # link proxy (typed FeaturePython)
  Detach = false
  LinkTransform = true
  LinkedObject = -> Link006 [PolarPattern.Face262]
  _LinkVersion = 0
  _Parent = -> Elements
FEATURE [Part::FeaturePython] _Element040  # link proxy (typed FeaturePython)
  Detach = false
  LinkTransform = true
  LinkedObject = -> Link006 [PolarPattern.Vertex264]
  _LinkVersion = 0
  _Parent = -> Elements
FEATURE [Part::FeaturePython] _Element041  # link proxy (typed FeaturePython)
  Detach = false
  LinkTransform = true
  LinkedObject = -> Link005 [Pocket.Face7]
  _LinkVersion = 0
  _Parent = -> Elements
FEATURE [App::FeaturePython] Constraint025  label="PointInPlane003"  # WARN: FeaturePython — macro-defined, semantics opaque (R4)
  Disabled = false
  Group = -> [ElementLink049,ElementLink050]
  _ConstraintType = 3
  _LinkVersion = 0
  _Parent = -> Constraints
FEATURE [App::FeaturePython] ElementLink049  label="_Element042"  # link proxy (typed FeaturePython)
  LinkTransform = true
  LinkedObject = -> _Element042
  _LinkVersion = 0
  _Parent = -> Constraint025
FEATURE [Part::FeaturePython] _Element042  # link proxy (typed FeaturePython)
  Detach = false
  LinkTransform = true
  LinkedObject = -> Link005 [Pocket.Vertex6]
  _LinkVersion = 0
  _Parent = -> Elements
FEATURE [App::FeaturePython] ElementLink050  label="_Element043"  # link proxy (typed FeaturePython)
  LinkTransform = true
  LinkedObject = -> _Element043
  _LinkVersion = 0
  _Parent = -> Constraint025
FEATURE [Part::FeaturePython] _Element043  # link proxy (typed FeaturePython)
  Detach = false
  LinkTransform = true
  LinkedObject = -> Link006 [PolarPattern.Face4]
  _LinkVersion = 0
  _Parent = -> Elements
FEATURE [App::FeaturePython] Constraint026  label="AxialAlignment005"  # WARN: FeaturePython — macro-defined, semantics opaque (R4)
  Angle = 0
  AnglePitch = 0
  AngleRoll = 0
  Disabled = false
  Group = -> [ElementLink051,ElementLink052]
  LockAngle = false
  Multiply = false
  _ConstraintType = 36
  _LinkVersion = 0
  _Parent = -> Constraints
FEATURE [App::FeaturePython] ElementLink051  label="_Element044"  # link proxy (typed FeaturePython)
  LinkTransform = true
  LinkedObject = -> _Element044
  _LinkVersion = 0
  _Parent = -> Constraint026
FEATURE [Part::FeaturePython] _Element044  # link proxy (typed FeaturePython)
  Detach = false
  LinkTransform = true
  LinkedObject = -> Link [Chamfer.Face101]
  _LinkVersion = 0
  _Parent = -> Elements
FEATURE [App::FeaturePython] ElementLink052  label="_Element006"  # link proxy (typed FeaturePython)
  LinkTransform = true
  LinkedObject = -> _Element006
  _LinkVersion = 0
  _Parent = -> Constraint026
FEATURE [App::FeaturePython] Constraint027  label="PointInPlane"  # WARN: FeaturePython — macro-defined, semantics opaque (R4)
  Disabled = false
  Group = -> [ElementLink053,ElementLink054]
  _ConstraintType = 3
  _LinkVersion = 0
  _Parent = -> Constraints
FEATURE [App::FeaturePython] ElementLink053  label="_Element045"  # link proxy (typed FeaturePython)
  LinkTransform = true
  LinkedObject = -> _Element045
  _LinkVersion = 0
  _Parent = -> Constraint027
FEATURE [Part::FeaturePython] _Element045  # link proxy (typed FeaturePython)
  Detach = false
  LinkTransform = true
  LinkedObject = -> Link003 [Chamfer001.Vertex32]
  _LinkVersion = 0
  _Parent = -> Elements
FEATURE [App::FeaturePython] ElementLink054  label="_Element046"  # link proxy (typed FeaturePython)
  LinkTransform = true
  LinkedObject = -> _Element046
  _LinkVersion = 0
  _Parent = -> Constraint027
FEATURE [Part::FeaturePython] _Element046  # link proxy (typed FeaturePython)
  Detach = false
  LinkTransform = true
  LinkedObject = -> Link [Chamfer.Face1]
  _LinkVersion = 0
  _Parent = -> Elements
FEATURE [App::FeaturePython] Constraint028  label="PointInPlane004"  # WARN: FeaturePython — macro-defined, semantics opaque (R4)
  Disabled = false
  Group = -> [ElementLink055,ElementLink056]
  _ConstraintType = 3
  _LinkVersion = 0
  _Parent = -> Constraints
FEATURE [App::FeaturePython] ElementLink055  label="_Element047"  # link proxy (typed FeaturePython)
  LinkTransform = true
  LinkedObject = -> _Element047
  _LinkVersion = 0
  _Parent = -> Constraint028
FEATURE [Part::FeaturePython] _Element047  # link proxy (typed FeaturePython)
  Detach = false
  LinkTransform = true
  LinkedObject = -> Link003 [Chamfer001.Vertex15]
  _LinkVersion = 0
  _Parent = -> Elements
FEATURE [App::FeaturePython] ElementLink056  label="_Element048"  # link proxy (typed FeaturePython)
  LinkTransform = true
  LinkedObject = -> _Element048
  _LinkVersion = 0
  _Parent = -> Constraint028
FEATURE [Part::FeaturePython] _Element048  # link proxy (typed FeaturePython)
  Detach = false
  LinkTransform = true
  LinkedObject = -> Link001 [MultiTransform001.Face87]
  _LinkVersion = 0
  _Parent = -> Elements
---- part tulejka-sruby.FCStd = doc fcstd_06e5567c1162 ----
FCSTD DOCUMENT  (FreeCAD 2020.10.16R22739 +2665 (Git))
Label: tulejka-sruby
License: All rights reserved
LicenseURL: http://en.wikipedia.org/wiki/All_rights_reserved
objects: Sketcher::SketchObject×1, PartDesign::Pad×1, PartDesign::Chamfer×1, PartDesign::Body×1
note: 8 computed .brp shape members not serialized (recipe doc carries the construction recipe); baked Part::Feature solids carry a one-line shape summary decoded from their .brp

FEATURE [Sketcher::SketchObject] Sketch
  MapMode = 5
  Support = -> [XY_Plane]
  sketch-geometry (2):
    g0: Circle CenterX=0 CenterY=0 CenterZ=0 NormalX=0 NormalY=0 NormalZ=1 AngleXU=0 Radius=5.25
    g1: Circle CenterX=0 CenterY=0 CenterZ=0 NormalX=0 NormalY=0 NormalZ=1 AngleXU=0 Radius=7.25
  constraints (4):
    c: Coincident(g0,g-1)
    c: Coincident(g1,g0)
    c: Diameter(g0) = 10.5
    c: Diameter(g1) = 14.5
FEATURE [PartDesign::Pad] Pad
  ClaimChildren = false
  Direction = (1,1,1)
  Length = 17
  Length2 = 100
  NewSolid = false
  Profile = -> Sketch
  Suppress = false
  Type = 0
FEATURE [PartDesign::Chamfer] Chamfer
  Angle = 45
  Base = -> Pad [Edge3]
  BaseFeature = -> Pad
  ChamferType = 0
  FlipDirection = false
  NewSolid = false
  Size = 1
  Size2 = 1
  SupportTransform = true
  Suppress = false
FEATURE [PartDesign::Body] Body  label="tulejka-sruby"
  ExportMode = 0
  Group = -> [Sketch,Pad,Chamfer]
  Origin = -> Origin
  Tip = -> Chamfer
  _ExportChildren = -> [Pad,Chamfer]
  _GroupVersion = 1
